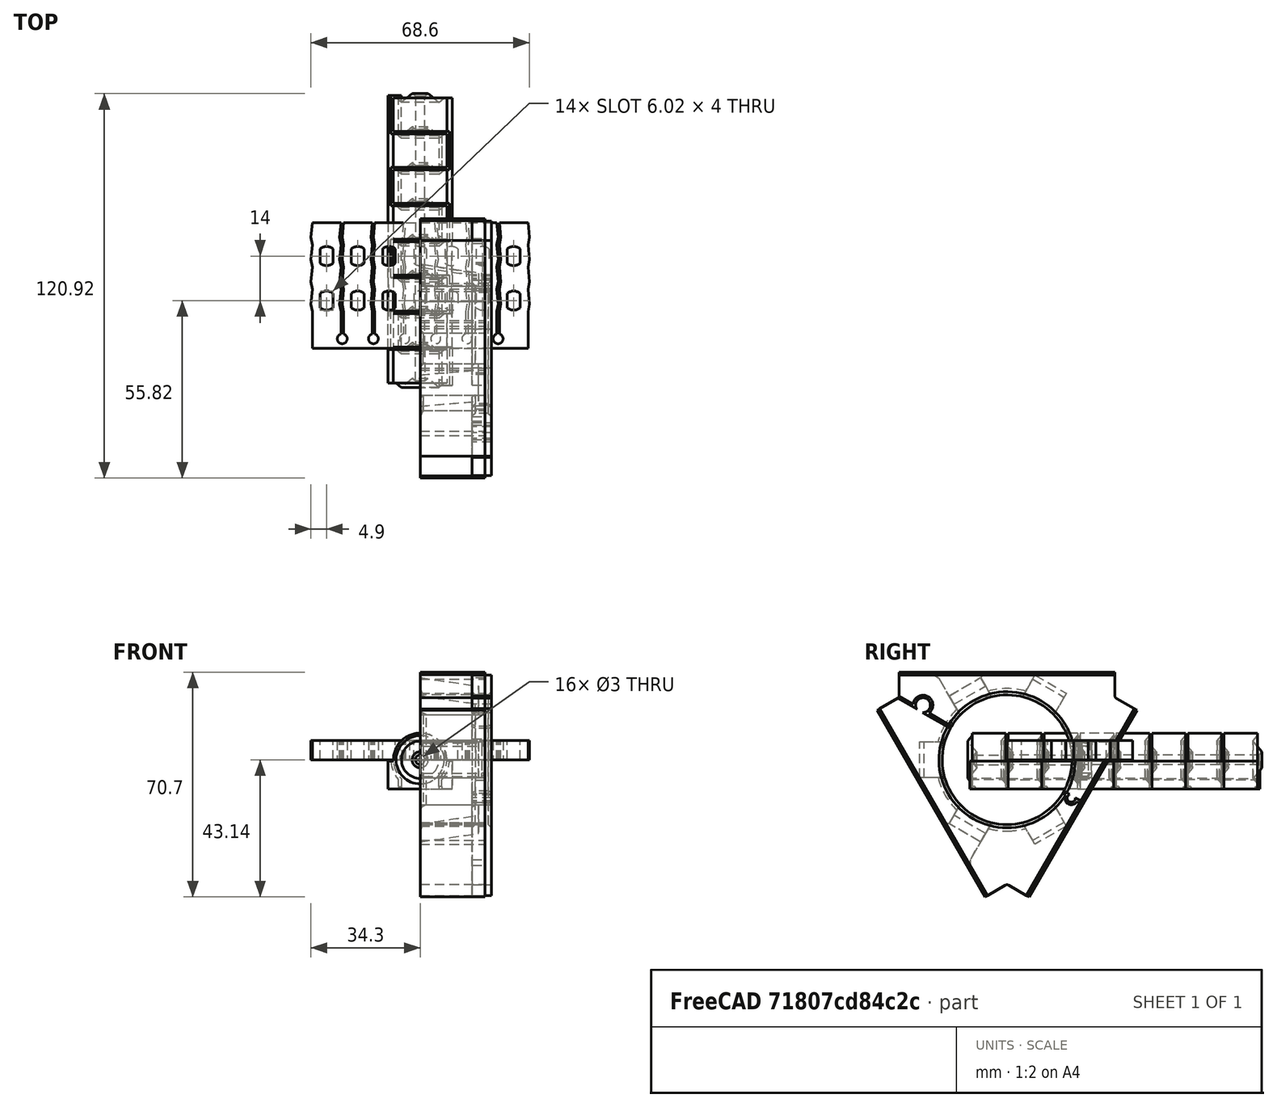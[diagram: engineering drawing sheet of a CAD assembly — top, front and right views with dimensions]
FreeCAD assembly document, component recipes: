
FREECAD ASSEMBLY — COMPONENT RECIPES ("BaseHingeModel_ver1.2_AxisFixator")

This assembly document has 8 components, labeled P0..P7 below (a component is one placed body or linked part). 7 of them carry a construction recipe — the FreeCAD feature program that regenerates the part from scratch, quoted from this document or its linked companion documents; the rest are supplied as boundary geometry only. No exploded tour is included for this assembly.
COMPONENT P0 — geometry summary ("Assembly"; no construction recipe available for this part):
  bounding box: 182.8 x 158.8 x 20.4 mm
  tessellated surface: 20,696 triangles
  volume: 9578097130411803656351970426578674498653964242418576373807381627235447409514995756881183408189511817567906541525464308833607482709359269325981809199022080 mm^3 (1616738801575943140395693637715189882977871249383409942478852649766611869419882643060896964713126329768861879254438412431142423713072396559864123359232% of its bounding box)
COMPONENT P1 — recipe-attached ("BaseHingePart", modeled in this document).
Construction recipe (the document's own serialized feature program — sketch geometry with constraints, then the solid features built on it; lengths are millimeters unless a unit is written):

FEATURE [Sketcher::SketchObject] Sketch007  label="RightCylinderScatch"
  FullyConstrained = true
  MapMode = 5
  Support = -> [XY_Plane002]
  expr: Constraints[10] = Spreadsheet.mmDiskHight
  expr: Constraints[11] = Spreadsheet.mmLedgeStep
  expr: Constraints[12] = Spreadsheet.mmLedgeStep * 2
  expr: Constraints[13] = Spreadsheet.mmLedgeStep
  expr: Constraints[14] = Spreadsheet.mmLedgeStep / 2
  expr: Constraints[16] = Spreadsheet.mmDiskLedge
  expr: Constraints[20] = Spreadsheet.mmDiskLedge * 2
  expr: Constraints[21] = Spreadsheet.mmDiskLedge
  expr: Constraints[34] = Spreadsheet.mmAirSpace / 2
  expr: Constraints[35] = Spreadsheet.mmLedgeStep / 2
  sketch-geometry (12):
    g0: LineSegment StartX=0 StartY=10.9 StartZ=0 EndX=0.84 EndY=10.9 EndZ=0
    g1: LineSegment StartX=0.84 StartY=10.9 StartZ=0 EndX=2.52 EndY=12.3 EndZ=0
    g2: LineSegment StartX=2.52 StartY=12.3 StartZ=0 EndX=5.88 EndY=9.5 EndZ=0
    g3: LineSegment StartX=5.88 StartY=9.5 StartZ=0 EndX=7.56 EndY=10.9 EndZ=0
    g4: LineSegment StartX=7.56 StartY=10.9 StartZ=0 EndX=8.4 EndY=10.9 EndZ=0
    g5: LineSegment StartX=5.88 StartY=-1 StartZ=0 EndX=2.52 EndY=1.8 EndZ=0
    g6: LineSegment StartX=2.52 StartY=1.8 StartZ=0 EndX=0.84 EndY=0.4 EndZ=0
    g7: LineSegment StartX=0.84 StartY=0.4 StartZ=0 EndX=0 EndY=0.4 EndZ=0
    g8: LineSegment StartX=0 StartY=0.4 StartZ=0 EndX=0 EndY=10.9 EndZ=0
    g9: LineSegment StartX=8.4 StartY=0.4 StartZ=0 EndX=7.56 EndY=0.4 EndZ=0
    g10: LineSegment StartX=7.56 StartY=0.4 StartZ=0 EndX=5.88 EndY=-1 EndZ=0
    g11: LineSegment StartX=8.4 StartY=10.9 StartZ=0 EndX=8.4 EndY=0.4 EndZ=0
  constraints (38):
    c: PointOnObject(g0,g-2)
    c: Horizontal(g0)
    c: Coincident(g0,g1)
    c: Coincident(g1,g2)
    c: Coincident(g2,g3)
    c: Coincident(g3,g4)
    c: Horizontal(g4)
    c: Coincident(g5,g6)
    c: Horizontal(g7)
    c: Coincident(g7,g8)
    c: DistanceY(g7,g0) = 10.5
    c: DistanceX(g0,g1) = 1.68
    c: DistanceX(g1,g2) = 3.36
    c: DistanceX(g2,g3) = 1.68
    c: DistanceX(g3,g4) = 0.84
    c: Coincident(g6,g7)
    c: DistanceY(g0,g1) = 1.4
    c: Equal(g0,g7)
    c: Equal(g1,g6)
    c: Coincident(g0,g8)
    c: DistanceY(g2,g1) = 2.8
    c: DistanceY(g2,g3) = 1.4
    c: Parallel(g2,g5)
    c: Coincident(g9,g10)
    c: Coincident(g10,g5)
    c: Parallel(g3,g10)
    c: Equal(g4,g9)
    c: Horizontal(g9)
    c: Vertical(g2,g5)
    c: Parallel(g1,g6)
    c: Vertical(g8)
    c: Coincident(g11,g4)
    c: Coincident(g11,g9)
    c: Vertical(g11)
    c: DistanceY(g-1,g7) = 0.4
    c: DistanceX(g-1,g0) = 0.84
    c: DistanceX(g-1,g0) = 0
    c: Vertical(g1,g5)
FEATURE [Sketcher::SketchObject] Sketch011  label="LeftCylinderScatch"
  FullyConstrained = true
  MapMode = 5
  Support = -> [XY_Plane]
  expr: Constraints[10] = Spreadsheet.mmLedgeStep
  expr: Constraints[11] = Spreadsheet.mmLedgeStep * 2
  expr: Constraints[12] = Spreadsheet.mmLedgeStep
  expr: Constraints[13] = Spreadsheet.mmLedgeStep / 2
  expr: Constraints[15] = Spreadsheet.mmDiskLedge
  expr: Constraints[19] = Spreadsheet.mmDiskLedge * 2
  expr: Constraints[20] = Spreadsheet.mmDiskLedge
  expr: Constraints[33] = Spreadsheet.mmAirSpace / 2
  expr: Constraints[34] = Spreadsheet.mmLedgeStep / 2
  expr: Constraints[9] = Spreadsheet.mmDiskHight
  sketch-geometry (12):
    g0: LineSegment StartX=0 StartY=-0.4 StartZ=0 EndX=0.84 EndY=-0.4 EndZ=0
    g1: LineSegment StartX=0.84 StartY=-0.4 StartZ=0 EndX=2.52 EndY=1 EndZ=0
    g2: LineSegment StartX=2.52 StartY=1 StartZ=0 EndX=5.88 EndY=-1.8 EndZ=0
    g3: LineSegment StartX=5.88 StartY=-1.8 StartZ=0 EndX=7.56 EndY=-0.4 EndZ=0
    g4: LineSegment StartX=7.56 StartY=-0.4 StartZ=0 EndX=8.4 EndY=-0.4 EndZ=0
    g5: LineSegment StartX=5.88 StartY=-12.3 StartZ=0 EndX=2.52 EndY=-9.5 EndZ=0
    g6: LineSegment StartX=2.52 StartY=-9.5 StartZ=0 EndX=0.84 EndY=-10.9 EndZ=0
    g7: LineSegment StartX=0.84 StartY=-10.9 StartZ=0 EndX=0 EndY=-10.9 EndZ=0
    g8: LineSegment StartX=0 StartY=-10.9 StartZ=0 EndX=0 EndY=-0.4 EndZ=0
    g9: LineSegment StartX=8.4 StartY=-10.9 StartZ=0 EndX=7.56 EndY=-10.9 EndZ=0
    g10: LineSegment StartX=7.56 StartY=-10.9 StartZ=0 EndX=5.88 EndY=-12.3 EndZ=0
    g11: LineSegment StartX=8.4 StartY=-0.4 StartZ=0 EndX=8.4 EndY=-10.9 EndZ=0
  constraints (36):
    c: Horizontal(g0)
    c: Coincident(g0,g1)
    c: Coincident(g1,g2)
    c: Coincident(g2,g3)
    c: Coincident(g3,g4)
    c: Horizontal(g4)
    c: Coincident(g5,g6)
    c: Horizontal(g7)
    c: Coincident(g7,g8)
    c: DistanceY(g7,g0) = 10.5
    c: DistanceX(g0,g1) = 1.68
    c: DistanceX(g1,g2) = 3.36
    c: DistanceX(g2,g3) = 1.68
    c: DistanceX(g3,g4) = 0.84
    c: Coincident(g6,g7)
    c: DistanceY(g0,g1) = 1.4
    c: Equal(g0,g7)
    c: Equal(g1,g6)
    c: Coincident(g0,g8)
    c: DistanceY(g2,g1) = 2.8
    c: DistanceY(g2,g3) = 1.4
    c: Parallel(g2,g5)
    c: Coincident(g9,g10)
    c: Coincident(g10,g5)
    c: Parallel(g3,g10)
    c: Equal(g4,g9)
    c: Horizontal(g9)
    c: Vertical(g2,g5)
    c: Parallel(g1,g6)
    c: Vertical(g8)
    c: Coincident(g11,g4)
    c: Coincident(g11,g9)
    c: Vertical(g11)
    c: DistanceY(g0,g-1) = 0.4
    c: DistanceX(g-1,g0) = 0.84
    c: DistanceX(g-1,g0) = 0
FEATURE [PartDesign::Revolution] Revolution  label="RightCylinderRevolution"
  Angle = 360
  Axis = (0,1,0)
  Base = (0,0,0)
  Profile = -> Sketch007
  ReferenceAxis = -> Sketch007 [V_Axis]
  Reversed = true
FEATURE [PartDesign::Revolution] Revolution004  label="LeftCylinderRevolution"
  Angle = 360
  Axis = (0,1,0)
  Base = (0,0,0)
  Profile = -> Sketch011
  ReferenceAxis = -> Sketch011 [V_Axis]
  Reversed = true
FEATURE [Sketcher::SketchObject] Sketch013  label="RightCylinderAxisHoleScatch"
  AttachmentOffset = pos=(0,0,1) rot=(0,0,1;0rad)
  FullyConstrained = true
  MapMode = 5
  Placement = pos=(0,-1,-2e-16) rot=(1,0,0;1.5708rad)
  Support = -> [XZ_Plane002]
  expr: .AttachmentOffset.Base.z = Spreadsheet.mmDiskLedge - Spreadsheet.mmAirSpace / 2
  expr: Constraints[1] = Spreadsheet.mmHoleRadius * 2
  sketch-geometry (1):
    g0: Circle CenterX=0 CenterY=0 CenterZ=0 NormalX=0 NormalY=0 NormalZ=1 AngleXU=0 Radius=1.5
  constraints (2):
    c: Coincident(g0,g-1)
    c: Diameter(g0) = 3
FEATURE [PartDesign::Pocket] Pocket001  label="RightCylinderAxisHole"
  BaseFeature = -> Revolution
  Direction = (0,1,2e-16)
  Length = 23.8
  Length2 = 5
  Profile = -> Sketch013
  ReferenceAxis = -> Sketch013 [N_Axis]
  Type = 0
  expr: Length = 2 * Spreadsheet.mmDiskHight + 2 * Spreadsheet.mmDiskLedge
FEATURE [Sketcher::SketchObject] Sketch014  label="LeftCylinderAxisHoleScatch"
  AttachmentOffset = pos=(0,0,-1) rot=(0,0,1;0rad)
  FullyConstrained = true
  MapMode = 5
  Placement = pos=(0,1,2e-16) rot=(1,0,0;1.5708rad)
  Support = -> [XZ_Plane]
  expr: .AttachmentOffset.Base.z = -(Spreadsheet.mmDiskLedge - Spreadsheet.mmAirSpace / 2)
  expr: Constraints[1] = Spreadsheet.mmHoleRadius * 2
  sketch-geometry (1):
    g0: Circle CenterX=0 CenterY=0 CenterZ=0 NormalX=0 NormalY=0 NormalZ=1 AngleXU=0 Radius=1.5
  constraints (2):
    c: Coincident(g0,g-1)
    c: Diameter(g0) = 3
FEATURE [PartDesign::Pocket] Pocket002  label="LeftCylinderAxisHole"
  BaseFeature = -> Revolution004
  Direction = (0,1,2e-16)
  Length = 21
  Length2 = 5
  Profile = -> Sketch014
  ReferenceAxis = -> Sketch014 [N_Axis]
  Reversed = true
  Type = 0
  expr: Length = Spreadsheet.mmDiskHight * 2
FEATURE [Sketcher::SketchObject] Sketch023  label="RightCylinderConnectedWingScatch"
  AttachmentOffset = pos=(0,0,-0.4) rot=(0,0,1;0rad)
  FullyConstrained = false
  MapMode = 5
  Placement = pos=(0,0.4,1e-16) rot=(1,0,0;1.5708rad)
  Support = -> [XZ_Plane002]
  expr: .AttachmentOffset.Base.z = -Spreadsheet.mmAirSpace / 2
  expr: Constraints[11] = Spreadsheet.mmHingeRadius + Spreadsheet.mmAirSpace
  expr: Constraints[17] = Spreadsheet.mmHingeRadius + Spreadsheet.mmAirSpace
  expr: Constraints[4] = Spreadsheet.mmHingeRadius * 2
  expr: Constraints[7] = Spreadsheet.mmHingeRadius / 5
  expr: Constraints[8] = Spreadsheet.mmAirSpace / 2
  sketch-geometry (9):
    g0: LineSegment StartX=-5.9397 StartY=-9.2 StartZ=0 EndX=10.0705 EndY=-9.2 EndZ=0
    g1: LineSegment StartX=10.0705 StartY=-9.2 StartZ=0 EndX=10.0705 EndY=-0.4 EndZ=0
    g2: LineSegment StartX=10.0705 StartY=-0.4 StartZ=0 EndX=8.39047 EndY=-0.4 EndZ=0
    g3: ArcOfCircle CenterX=0 CenterY=9e-16 CenterZ=0 NormalX=0 NormalY=0 NormalZ=1 AngleXU=0 Radius=8.4 StartAngle=3.92699 EndAngle=6.23555
    g4: LineSegment StartX=-10.8949 StartY=25.2528 StartZ=0 EndX=-10.8949 EndY=-29.472 EndZ=0
    g5: LineSegment StartX=0 StartY=0 StartZ=0 EndX=8.39047 EndY=-0.4 EndZ=0
    g6: LineSegment StartX=-5.9397 StartY=-5.9397 StartZ=0 EndX=-5.9397 EndY=-9.2 EndZ=0
    g7: LineSegment StartX=0 StartY=9e-16 StartZ=0 EndX=-20.2547 EndY=-20.2547 EndZ=0
    g8: LineSegment StartX=-5.9397 StartY=-5.9397 StartZ=0 EndX=-5.9397 EndY=-9.42884 EndZ=0
  constraints (24):
    c: Coincident(g0,g1)
    c: Vertical(g1)
    c: Horizontal(g2)
    c: Vertical(g4)
    c: Diameter(g3) = 16.8
    c: Coincident(g2,g1)
    c: Coincident(g5,g2)
    c: DistanceX(g2,g2) = 1.68
    c: DistanceY(g1,g-1) = 0.4
    c: Coincident(g3,g6)
    c: Coincident(g3,g2)
    c: DistanceY(g0,g3) = 9.2
    c: PointOnObject(g3,g7)
    c: Coincident(g7,g3)
    c: Angle(g-2,g7) = 2.35619
    c: PointOnObject(g3,g-2)
    c: Horizontal(g0)
    c: DistanceY(g0,g-1) = 9.2
    c: Vertical(g8)
    c: PointOnObject(g8,g7)
    c: PointOnObject(g8,g3)
    c: PointOnObject(g6,g8)
    c: PointOnObject(g0,g8)
    c: PointOnObject(g6,g0)
FEATURE [PartDesign::Pad] Pad008  label="RightCylinderConnectedWingBody"
  BaseFeature = -> Pocket001
  Direction = (0,-1,-2e-16)
  Length = 10.5
  Length2 = 10
  Profile = -> Sketch023
  ReferenceAxis = -> Sketch023 [N_Axis]
  Reversed = true
  Type = 0
  expr: Length = Spreadsheet.mmDiskHight
FEATURE [Sketcher::SketchObject] Sketch024  label="RightCylinderDisconnectedWingScatch"
  AttachmentOffset = pos=(0,0,0.4) rot=(0,0,1;0rad)
  FullyConstrained = false
  MapMode = 5
  Placement = pos=(0,-0.4,-1e-16) rot=(1,0,0;1.5708rad)
  Support = -> [XZ_Plane002]
  expr: .AttachmentOffset.Base.z = Spreadsheet.mmAirSpace / 2
  expr: Constraints[10] = Spreadsheet.mmHingeRadius * 6 / 5
  expr: Constraints[14] = (Spreadsheet.mmHingeRadius + Spreadsheet.mmAirSpace) * 2
  expr: Constraints[18] = Spreadsheet.mmAirSpace
  expr: Constraints[26] = Spreadsheet.mmAirSpace
  expr: Constraints[29] = Spreadsheet.mmHingeRadius * 2
  expr: Constraints[2] = (Spreadsheet.mmHingeRadius + Spreadsheet.mmAirSpace) * 2
  expr: Constraints[8] = Spreadsheet.mmHingeRadius + Spreadsheet.mmAirSpace
  expr: Constraints[9] = Spreadsheet.mmAirSpace / 2
  sketch-geometry (12):
    g0: Circle CenterX=0 CenterY=0 CenterZ=0 NormalX=0 NormalY=0 NormalZ=1 AngleXU=0 Radius=9.2
    g1: LineSegment StartX=-5.9397 StartY=-5.9397 StartZ=0 EndX=-5.9397 EndY=-9.59435 EndZ=0
    g2: LineSegment StartX=-10.08 StartY=-0.4 StartZ=0 EndX=-10.08 EndY=-9.2 EndZ=0
    g3: LineSegment StartX=-10.08 StartY=-9.2 StartZ=0 EndX=-5.9397 EndY=-9.2 EndZ=0
    g4: LineSegment StartX=-6.7397 StartY=-8.4 StartZ=0 EndX=-6.7397 EndY=-6.26231 EndZ=0
    g5: LineSegment StartX=-9.1913 StartY=-0.4 StartZ=0 EndX=-10.08 EndY=-0.4 EndZ=0
    g6: LineSegment StartX=0 StartY=0 StartZ=0 EndX=-7.18968 EndY=-7.18968 EndZ=0
    g7: ArcOfCircle CenterX=0 CenterY=0 CenterZ=0 NormalX=0 NormalY=0 NormalZ=1 AngleXU=0 Radius=9.2 StartAngle=3.18508 EndAngle=3.89029
    g8: LineSegment StartX=-6.7397 StartY=-9.55843 StartZ=0 EndX=-6.7397 EndY=-4.9559 EndZ=0
    g9: LineSegment StartX=-6.7397 StartY=-8.4 StartZ=0 EndX=-5.9397 EndY=-8.4 EndZ=0
    g10: LineSegment StartX=-5.9397 StartY=-8.4 StartZ=0 EndX=-5.9397 EndY=-9.2 EndZ=0
    g11: Circle CenterX=0 CenterY=0 CenterZ=0 NormalX=0 NormalY=0 NormalZ=1 AngleXU=0 Radius=8.4
  constraints (33):
    c: Coincident(g0,g-1)
    c: Vertical(g1)
    c: Diameter(g0) = 18.4
    c: Vertical(g2)
    c: Coincident(g2,g3)
    c: Horizontal(g3)
    c: Coincident(g5,g2)
    c: Horizontal(g5)
    c: DistanceY(g2,g-1) = 9.2
    c: DistanceY(g2,g-1) = 0.4
    c: DistanceX(g2,g0) = 10.08
    c: Coincident(g6,g0)
    c: Angle(g-2,g6) = 2.35619
    c: Coincident(g7,g0)
    c: Diameter(g7) = 18.4
    c: Coincident(g7,g4)
    c: Coincident(g7,g5)
    c: Vertical(g8)
    c: DistanceX(g8,g1) = 0.8
    c: Coincident(g4,g9)
    c: PointOnObject(g9,g1)
    c: Horizontal(g9)
    c: Coincident(g9,g10)
    c: PointOnObject(g10,g1)
    c: PointOnObject(g3,g1)
    c: PointOnObject(g10,g3)
    c: DistanceY(g3,g9) = 0.8
    c: PointOnObject(g4,g8)
    c: Coincident(g11,g7)
    c: Diameter(g11) = 16.8
    c: PointOnObject(g1,g11)
    c: PointOnObject(g1,g6)
    c: PointOnObject(g4,g8)
FEATURE [PartDesign::Pad] Pad009  label="RightCylinderDisconnectedWingBody"
  BaseFeature = -> Pad008
  Direction = (0,-1,-2e-16)
  Length = 12.1
  Length2 = 10
  Profile = -> Sketch024
  ReferenceAxis = -> Sketch024 [N_Axis]
  Reversed = true
  Type = 0
  expr: Length = Spreadsheet.mmDiskHight + Spreadsheet.mmAirSpace * 2
FEATURE [Sketcher::SketchObject] Sketch025  label="LeftCylinderConnectedWingScatch"
  AttachmentOffset = pos=(0,0,0.4) rot=(0,0,1;0rad)
  FullyConstrained = false
  MapMode = 5
  Placement = pos=(0,-0.4,-1e-16) rot=(1,0,0;1.5708rad)
  Support = -> [XZ_Plane]
  expr: .AttachmentOffset.Base.z = Spreadsheet.mmAirSpace / 2
  expr: Constraints[10] = Spreadsheet.mmAirSpace / 2
  expr: Constraints[11] = Spreadsheet.mmHingeRadius + Spreadsheet.mmAirSpace
  expr: Constraints[15] = Spreadsheet.mmHingeRadius * 2
  expr: Constraints[2] = Spreadsheet.mmHingeRadius * 2
  expr: Constraints[9] = Spreadsheet.mmHingeRadius * 6 / 5
  sketch-geometry (8):
    g0: LineSegment StartX=0 StartY=0 StartZ=0 EndX=8.8497 EndY=-8.8497 EndZ=0
    g1: Circle CenterX=0 CenterY=0 CenterZ=0 NormalX=0 NormalY=0 NormalZ=1 AngleXU=0 Radius=8.4
    g2: LineSegment StartX=-10.08 StartY=-0.4 StartZ=0 EndX=-10.08 EndY=-9.2 EndZ=0
    g3: LineSegment StartX=-10.08 StartY=-9.2 StartZ=0 EndX=5.9397 EndY=-9.2 EndZ=0
    g4: LineSegment StartX=5.9397 StartY=-9.2 StartZ=0 EndX=5.9397 EndY=-5.9397 EndZ=0
    g5: LineSegment StartX=-8.39047 StartY=-0.4 StartZ=0 EndX=-10.08 EndY=-0.4 EndZ=0
    g6: ArcOfCircle CenterX=0 CenterY=0 CenterZ=0 NormalX=0 NormalY=0 NormalZ=1 AngleXU=0 Radius=8.4 StartAngle=3.18923 EndAngle=5.49779
    g7: LineSegment StartX=5.9397 StartY=-5.9397 StartZ=0 EndX=5.9397 EndY=-9.58153 EndZ=0
  constraints (24):
    c: Coincident(g0,g-1)
    c: Coincident(g1,g0)
    c: Diameter(g1) = 16.8
    c: Vertical(g2)
    c: Coincident(g2,g3)
    c: Horizontal(g3)
    c: Coincident(g5,g2)
    c: Horizontal(g5)
    c: PointOnObject(g5,g1)
    c: DistanceX(g2,g0) = 10.08
    c: DistanceY(g2,g-1) = 0.4
    c: DistanceY(g2,g-1) = 9.2
    c: Angle(g0,g-2) = 2.35619
    c: PointOnObject(g4,g0)
    c: Coincident(g6,g0)
    c: Diameter(g6) = 16.8
    c: Coincident(g6,g5)
    c: Coincident(g6,g4)
    c: Vertical(g7)
    c: PointOnObject(g7,g1)
    c: PointOnObject(g7,g0)
    c: PointOnObject(g4,g7)
    c: PointOnObject(g3,g7)
    c: PointOnObject(g4,g3)
FEATURE [PartDesign::Pad] Pad010  label="LeftCylinderConnectedWingBody"
  BaseFeature = -> Pocket002
  Direction = (0,-1,-2e-16)
  Length = 10.5
  Length2 = 10
  Profile = -> Sketch025
  ReferenceAxis = -> Sketch025 [N_Axis]
  Type = 0
  expr: Length = Spreadsheet.mmDiskHight
FEATURE [Sketcher::SketchObject] Sketch026  label="LeftCylinderDisconnectedWingScatch"
  AttachmentOffset = pos=(0,0,-0.4) rot=(0,0,1;0rad)
  FullyConstrained = false
  MapMode = 5
  Placement = pos=(0,0.4,1e-16) rot=(1,0,0;1.5708rad)
  Support = -> [XZ_Plane]
  expr: .AttachmentOffset.Base.z = -Spreadsheet.mmAirSpace / 2
  expr: Constraints[10] = Spreadsheet.mmHingeRadius + Spreadsheet.mmAirSpace
  expr: Constraints[16] = Spreadsheet.mmAirSpace
  expr: Constraints[18] = (Spreadsheet.mmHingeRadius + Spreadsheet.mmAirSpace) * 2
  expr: Constraints[26] = Spreadsheet.mmAirSpace
  expr: Constraints[29] = Spreadsheet.mmHingeRadius * 2
  expr: Constraints[2] = (Spreadsheet.mmHingeRadius + Spreadsheet.mmAirSpace) * 2
  expr: Constraints[8] = Spreadsheet.mmAirSpace / 2
  expr: Constraints[9] = Spreadsheet.mmHingeRadius / 5 * 6
  sketch-geometry (12):
    g0: LineSegment StartX=0 StartY=0 StartZ=0 EndX=9.28474 EndY=-9.28474 EndZ=0
    g1: ArcOfCircle CenterX=0 CenterY=0 CenterZ=0 NormalX=0 NormalY=0 NormalZ=1 AngleXU=0 Radius=9.2 StartAngle=5.53449 EndAngle=6.23969
    g2: LineSegment StartX=9.1913 StartY=-0.4 StartZ=0 EndX=10.08 EndY=-0.4 EndZ=0
    g3: LineSegment StartX=10.08 StartY=-0.4 StartZ=0 EndX=10.08 EndY=-9.2 EndZ=0
    g4: LineSegment StartX=10.08 StartY=-9.2 StartZ=0 EndX=5.9397 EndY=-9.2 EndZ=0
    g5: LineSegment StartX=6.7397 StartY=-8.4 StartZ=0 EndX=6.7397 EndY=-6.26231 EndZ=0
    g6: LineSegment StartX=5.9397 StartY=-5.9397 StartZ=0 EndX=5.9397 EndY=-9.17966 EndZ=0
    g7: LineSegment StartX=6.7397 StartY=-5.451 StartZ=0 EndX=6.7397 EndY=-9.15329 EndZ=0
    g8: Circle CenterX=0 CenterY=0 CenterZ=0 NormalX=0 NormalY=0 NormalZ=1 AngleXU=0 Radius=9.2
    g9: LineSegment StartX=6.7397 StartY=-8.4 StartZ=0 EndX=5.9397 EndY=-8.4 EndZ=0
    g10: LineSegment StartX=5.9397 StartY=-8.4 StartZ=0 EndX=5.9397 EndY=-9.2 EndZ=0
    g11: Circle CenterX=0 CenterY=0 CenterZ=0 NormalX=0 NormalY=0 NormalZ=1 AngleXU=0 Radius=8.4
  constraints (33):
    c: Coincident(g0,g-1)
    c: Coincident(g1,g0)
    c: Diameter(g1) = 18.4
    c: Horizontal(g2)
    c: Coincident(g2,g3)
    c: Vertical(g3)
    c: Coincident(g3,g4)
    c: Horizontal(g4)
    c: DistanceY(g2,g-1) = 0.4
    c: DistanceX(g-1,g2) = 10.08
    c: DistanceY(g3,g-1) = 9.2
    c: Angle(g0,g-2) = 2.35619
    c: Coincident(g1,g2)
    c: Coincident(g1,g5)
    c: Vertical(g6)
    c: Vertical(g7)
    c: DistanceX(g6,g7) = 0.8
    c: Coincident(g8,g1)
    c: Diameter(g8) = 18.4
    c: PointOnObject(g5,g7)
    c: Coincident(g5,g9)
    c: PointOnObject(g9,g6)
    c: Horizontal(g9)
    c: Coincident(g9,g10)
    c: PointOnObject(g10,g6)
    c: PointOnObject(g4,g6)
    c: DistanceY(g4,g9) = 0.8
    c: PointOnObject(g10,g4)
    c: Coincident(g11,g1)
    c: Diameter(g11) = 16.8
    c: PointOnObject(g6,g11)
    c: PointOnObject(g6,g0)
    c: PointOnObject(g1,g7)
FEATURE [PartDesign::Pad] Pad011  label="LeftCylinderDisconnectedWingBody"
  BaseFeature = -> Pad010
  Direction = (0,-1,-2e-16)
  Length = 12.1
  Length2 = 10
  Profile = -> Sketch026
  ReferenceAxis = -> Sketch026 [N_Axis]
  Type = 0
  expr: Length = Spreadsheet.mmDiskHight + Spreadsheet.mmAirSpace * 2
FEATURE [Sketcher::SketchObject] Sketch046  label="LeftCylinderSeparatorScatch"
  AttachmentOffset = pos=(0,0,-0.4) rot=(0,0,1;0rad)
  FullyConstrained = false
  MapMode = 5
  Placement = pos=(0,0.4,1e-16) rot=(1,0,0;1.5708rad)
  Support = -> [XZ_Plane]
  expr: .AttachmentOffset.Base.z = -Spreadsheet.mmAirSpace / 2
  expr: Constraints[14] = Spreadsheet.mmAirSpace
  expr: Constraints[15] = Spreadsheet.mmHingeRadius * 2
  expr: Constraints[2] = Spreadsheet.mmHingeRadius + Spreadsheet.mmAirSpace
  expr: Constraints[6] = Spreadsheet.mmAirSpace
  expr: Constraints[7] = (Spreadsheet.mmHingeRadius + Spreadsheet.mmAirSpace) * 2
  sketch-geometry (9):
    g0: LineSegment StartX=0 StartY=0 StartZ=0 EndX=9.28922 EndY=-9.28922 EndZ=0
    g1: LineSegment StartX=6.7397 StartY=-9.2 StartZ=0 EndX=5.9397 EndY=-9.2 EndZ=0
    g2: LineSegment StartX=6.7397 StartY=-8.4 StartZ=0 EndX=6.7397 EndY=-9.2 EndZ=0
    g3: LineSegment StartX=5.9397 StartY=-5.9397 StartZ=0 EndX=5.9397 EndY=-8.88748 EndZ=0
    g4: LineSegment StartX=6.7397 StartY=-5.40605 StartZ=0 EndX=6.7397 EndY=-8.88997 EndZ=0
    g5: Circle CenterX=0 CenterY=0 CenterZ=0 NormalX=0 NormalY=0 NormalZ=1 AngleXU=0 Radius=9.2
    g6: LineSegment StartX=6.7397 StartY=-8.4 StartZ=0 EndX=5.9397 EndY=-8.4 EndZ=0
    g7: LineSegment StartX=5.9397 StartY=-8.4 StartZ=0 EndX=5.9397 EndY=-9.2 EndZ=0
    g8: Circle CenterX=0 CenterY=0 CenterZ=0 NormalX=0 NormalY=0 NormalZ=1 AngleXU=0 Radius=8.4
  constraints (23):
    c: Coincident(g0,g-1)
    c: Horizontal(g1)
    c: DistanceY(g1,g-1) = 9.2
    c: Angle(g0,g-2) = 2.35619
    c: Vertical(g3)
    c: Vertical(g4)
    c: DistanceX(g3,g4) = 0.8
    c: Diameter(g5) = 18.4
    c: PointOnObject(g2,g4)
    c: Coincident(g2,g6)
    c: PointOnObject(g6,g3)
    c: Horizontal(g6)
    c: Coincident(g6,g7)
    c: PointOnObject(g7,g3)
    c: DistanceY(g1,g6) = 0.8
    c: Diameter(g8) = 16.8
    c: PointOnObject(g3,g8)
    c: PointOnObject(g3,g0)
    c: PointOnObject(g1,g4)
    c: Coincident(g2,g1)
    c: Coincident(g0,g8)
    c: Coincident(g0,g5)
    c: Coincident(g7,g1)
FEATURE [PartDesign::Pocket] Pocket004  label="LeftCylinderSeparator"
  BaseFeature = -> Pad011
  Direction = (0,1,2e-16)
  Length = 10.5
  Length2 = 5
  Profile = -> Sketch046
  ReferenceAxis = -> Sketch046 [N_Axis]
  Reversed = true
  Type = 0
  expr: Length = Spreadsheet.mmDiskHight
FEATURE [PartDesign::Body] Body  label="LeftCylinder"
  Group = -> [Sketch011,Revolution004,Sketch014,Pocket002,Sketch025,Pad010,Sketch026,Pad011,Sketch046,Pocket004]
  Origin = -> Origin
  Tip = -> Pocket004
FEATURE [Sketcher::SketchObject] Sketch047  label="RightCylinderSeparatorScatch"
  AttachmentOffset = pos=(0,0,0.4) rot=(0,0,1;0rad)
  FullyConstrained = false
  MapMode = 5
  Placement = pos=(0,-0.4,-1e-16) rot=(1,0,0;1.5708rad)
  Support = -> [XZ_Plane002]
  expr: .AttachmentOffset.Base.z = Spreadsheet.mmAirSpace / 2
  expr: Constraints[15] = Spreadsheet.mmAirSpace
  expr: Constraints[17] = Spreadsheet.mmHingeRadius * 2
  expr: Constraints[2] = (Spreadsheet.mmHingeRadius + Spreadsheet.mmAirSpace) * 2
  expr: Constraints[4] = Spreadsheet.mmHingeRadius + Spreadsheet.mmAirSpace
  expr: Constraints[8] = Spreadsheet.mmAirSpace
  sketch-geometry (9):
    g0: Circle CenterX=0 CenterY=0 CenterZ=0 NormalX=0 NormalY=0 NormalZ=1 AngleXU=0 Radius=9.2
    g1: LineSegment StartX=-5.9397 StartY=-5.9397 StartZ=0 EndX=-5.9397 EndY=-9.59435 EndZ=0
    g2: LineSegment StartX=-6.7397 StartY=-9.2 StartZ=0 EndX=-5.9397 EndY=-9.2 EndZ=0
    g3: LineSegment StartX=0 StartY=0 StartZ=0 EndX=-7.19425 EndY=-7.19425 EndZ=0
    g4: LineSegment StartX=-6.7397 StartY=-9.55843 StartZ=0 EndX=-6.7397 EndY=-4.9559 EndZ=0
    g5: LineSegment StartX=-6.7397 StartY=-8.4 StartZ=0 EndX=-5.9397 EndY=-8.4 EndZ=0
    g6: LineSegment StartX=-5.9397 StartY=-8.4 StartZ=0 EndX=-5.9397 EndY=-9.2 EndZ=0
    g7: Circle CenterX=0 CenterY=0 CenterZ=0 NormalX=0 NormalY=0 NormalZ=1 AngleXU=0 Radius=8.4
    g8: LineSegment StartX=-6.7397 StartY=-8.4 StartZ=0 EndX=-6.7397 EndY=-9.2 EndZ=0
  constraints (24):
    c: Coincident(g0,g-1)
    c: Vertical(g1)
    c: Diameter(g0) = 18.4
    c: Horizontal(g2)
    c: DistanceY(g2,g-1) = 9.2
    c: Coincident(g3,g0)
    c: Angle(g-2,g3) = 2.35619
    c: Vertical(g4)
    c: DistanceX(g4,g1) = 0.8
    c: PointOnObject(g5,g1)
    c: Horizontal(g5)
    c: Coincident(g5,g6)
    c: PointOnObject(g6,g1)
    c: PointOnObject(g2,g1)
    c: PointOnObject(g6,g2)
    c: DistanceY(g2,g5) = 0.8
    c: PointOnObject(g5,g4)
    c: Diameter(g7) = 16.8
    c: PointOnObject(g1,g7)
    c: PointOnObject(g1,g3)
    c: PointOnObject(g2,g4)
    c: Coincident(g8,g5)
    c: Coincident(g8,g2)
    c: Coincident(g0,g7)
FEATURE [PartDesign::Pocket] Pocket005  label="RightCylinderSeparator"
  BaseFeature = -> Pad009
  Direction = (0,1,2e-16)
  Length = 10.5
  Length2 = 5
  Profile = -> Sketch047
  ReferenceAxis = -> Sketch047 [N_Axis]
  Type = 0
  expr: Length = Spreadsheet.mmDiskHight
FEATURE [PartDesign::Body] Body001  label="RightCylinder"
  Group = -> [Sketch007,Revolution,Sketch013,Pocket001,Sketch023,Pad008,Sketch024,Pad009,Sketch047,Pocket005]
  Origin = -> Origin002
  Tip = -> Pocket005
COMPONENT P2 — recipe-attached ("BeamFixatoPart", modeled in this document).
Construction recipe (the document's own serialized feature program — sketch geometry with constraints, then the solid features built on it; lengths are millimeters unless a unit is written):

FEATURE [Sketcher::SketchObject] Sketch022  label="FixatorBodySketch"
  FullyConstrained = false
  MapMode = 5
  Support = -> [XY_Plane005]
  expr: Constraints[143] = Spreadsheet.mmCellWall
  expr: Constraints[144] = Spreadsheet.mmCellWall
  expr: Constraints[145] = Spreadsheet.mmCellWall
  expr: Constraints[146] = Spreadsheet.mmCellWidth
  expr: Constraints[147] = Spreadsheet.mmCellWidth
  expr: Constraints[148] = Spreadsheet.mmCellWidth
  expr: Constraints[169] = Spreadsheet.mmCommonBaseLenght
  expr: Constraints[170] = Spreadsheet.mmToothStep
  expr: Constraints[171] = Spreadsheet.mmToothStep
  expr: Constraints[172] = Spreadsheet.mmToothStep
  expr: Constraints[173] = Spreadsheet.mmToothStep
  expr: Constraints[174] = Spreadsheet.mmToothStep
  expr: Constraints[183] = Spreadsheet.mmCellWall * 3
  expr: Constraints[184] = Spreadsheet.mmCellWall * 3
  expr: Constraints[185] = Spreadsheet.mmCellWall * 3
  expr: Constraints[186] = Spreadsheet.mmCellWall * 3
  expr: Constraints[425] = Spreadsheet.mmFirstCircleArcToBase
  expr: Constraints[435] = Spreadsheet.mmCellWall / 2
  expr: Constraints[464] = Spreadsheet.mmCellWidth + Spreadsheet.mmCellWall
  expr: Constraints[5] = Spreadsheet.mmBaseWidth
  expr: Constraints[6] = Spreadsheet.mmBaseEnd
  sketch-geometry (155):
    g0: LineSegment StartX=-33.9 StartY=0 StartZ=0 EndX=-33.9 EndY=39.5 EndZ=0
    g1: LineSegment StartX=-33.9 StartY=39.5 StartZ=0 EndX=33.9 EndY=39.5 EndZ=0
    g2: LineSegment StartX=33.9 StartY=39.5 StartZ=0 EndX=33.9 EndY=0 EndZ=0
    g3: LineSegment StartX=-73.1099 StartY=25.5 StartZ=0 EndX=65.6354 EndY=25.5 EndZ=0
    g4: LineSegment StartX=-33.9 StartY=0 StartZ=0 EndX=-33.9 EndY=11.5 EndZ=0
    g5: LineSegment StartX=-33.9 StartY=11.5 StartZ=0 EndX=-34.3 EndY=13.9 EndZ=0
    g6: LineSegment StartX=-34.3 StartY=13.9 StartZ=0 EndX=-33.9 EndY=18.5 EndZ=0
    g7: LineSegment StartX=-33.9 StartY=18.5 StartZ=0 EndX=-34.3 EndY=20.9 EndZ=0
    g8: LineSegment StartX=-34.3 StartY=20.9 StartZ=0 EndX=-33.9 EndY=25.5 EndZ=0
    g9: LineSegment StartX=-33.9 StartY=25.5 StartZ=0 EndX=-34.3 EndY=27.9 EndZ=0
    g10: LineSegment StartX=-34.3 StartY=27.9 StartZ=0 EndX=-33.9 EndY=32.5 EndZ=0
    g11: LineSegment StartX=-33.9 StartY=32.5 StartZ=0 EndX=-34.3 EndY=34.9 EndZ=0
    g12: LineSegment StartX=-34.3 StartY=34.9 StartZ=0 EndX=-33.9 EndY=39.5 EndZ=0
    g13: LineSegment StartX=-33.9 StartY=39.5 StartZ=0 EndX=-24.9 EndY=39.5 EndZ=0
    g14: LineSegment StartX=-24.9 StartY=39.5 StartZ=0 EndX=-25.3 EndY=34.9 EndZ=0
    g15: LineSegment StartX=-25.3 StartY=34.9 StartZ=0 EndX=-24.9 EndY=32.5 EndZ=0
    g16: LineSegment StartX=-24.9 StartY=32.5 StartZ=0 EndX=-25.3 EndY=27.9 EndZ=0
    g17: LineSegment StartX=-25.3 StartY=27.9 StartZ=0 EndX=-24.9 EndY=25.5 EndZ=0
    g18: LineSegment StartX=-24.9 StartY=25.5 StartZ=0 EndX=-25.3 EndY=20.9 EndZ=0
    g19: LineSegment StartX=-25.3 StartY=20.9 StartZ=0 EndX=-24.9 EndY=18.5 EndZ=0
    g20: LineSegment StartX=-24.9 StartY=18.5 StartZ=0 EndX=-25.3 EndY=13.9 EndZ=0
    g21: LineSegment StartX=-25.3 StartY=13.9 StartZ=0 EndX=-24.9 EndY=11.5 EndZ=0
    g22: LineSegment StartX=-24.9 StartY=11.5 StartZ=0 EndX=-24.9 EndY=4.5 EndZ=0
    g23: LineSegment StartX=-24.1 StartY=4.5 StartZ=0 EndX=-24.1 EndY=11.5 EndZ=0
    g24: LineSegment StartX=-24.1 StartY=11.5 StartZ=0 EndX=-24.5 EndY=13.9 EndZ=0
    g25: LineSegment StartX=-24.5 StartY=13.9 StartZ=0 EndX=-24.1 EndY=18.5 EndZ=0
    g26: LineSegment StartX=-24.1 StartY=18.5 StartZ=0 EndX=-24.5 EndY=20.9 EndZ=0
    g27: LineSegment StartX=-24.5 StartY=20.9 StartZ=0 EndX=-24.1 EndY=25.5 EndZ=0
    g28: LineSegment StartX=-24.1 StartY=25.5 StartZ=0 EndX=-24.5 EndY=27.9 EndZ=0
    g29: LineSegment StartX=-24.5 StartY=27.9 StartZ=0 EndX=-24.1 EndY=32.5 EndZ=0
    g30: LineSegment StartX=-24.1 StartY=32.5 StartZ=0 EndX=-24.5 EndY=34.9 EndZ=0
    g31: LineSegment StartX=-24.5 StartY=34.9 StartZ=0 EndX=-24.1 EndY=39.5 EndZ=0
    g32: LineSegment StartX=-24.1 StartY=39.5 StartZ=0 EndX=-15.1 EndY=39.5 EndZ=0
    g33: LineSegment StartX=-15.1 StartY=39.5 StartZ=0 EndX=-15.5 EndY=34.9 EndZ=0
    g34: LineSegment StartX=-15.5 StartY=34.9 StartZ=0 EndX=-15.1 EndY=32.5 EndZ=0
    g35: LineSegment StartX=-15.1 StartY=32.5 StartZ=0 EndX=-15.5 EndY=27.9 EndZ=0
    g36: LineSegment StartX=-15.5 StartY=27.9 StartZ=0 EndX=-15.1 EndY=25.5 EndZ=0
    g37: LineSegment StartX=-15.1 StartY=25.5 StartZ=0 EndX=-15.5 EndY=20.9 EndZ=0
    g38: LineSegment StartX=-15.5 StartY=20.9 StartZ=0 EndX=-15.1 EndY=18.5 EndZ=0
    g39: LineSegment StartX=-15.1 StartY=18.5 StartZ=0 EndX=-15.5 EndY=13.9 EndZ=0
    g40: LineSegment StartX=-15.5 StartY=13.9 StartZ=0 EndX=-15.1 EndY=11.5 EndZ=0
    g41: LineSegment StartX=-15.1 StartY=11.5 StartZ=0 EndX=-15.1 EndY=4.5 EndZ=0
    g42: LineSegment StartX=-14.3 StartY=4.5 StartZ=0 EndX=-14.3 EndY=11.5 EndZ=0
    g43: LineSegment StartX=-14.3 StartY=11.5 StartZ=0 EndX=-14.7 EndY=13.9 EndZ=0
    g44: LineSegment StartX=-14.7 StartY=13.9 StartZ=0 EndX=-14.3 EndY=18.5 EndZ=0
    g45: LineSegment StartX=-14.3 StartY=18.5 StartZ=0 EndX=-14.7 EndY=20.9 EndZ=0
    g46: LineSegment StartX=-14.7 StartY=20.9 StartZ=0 EndX=-14.3 EndY=25.5 EndZ=0
    g47: LineSegment StartX=-14.3 StartY=25.5 StartZ=0 EndX=-14.7 EndY=27.9 EndZ=0
    g48: LineSegment StartX=-14.7 StartY=27.9 StartZ=0 EndX=-14.3 EndY=32.5 EndZ=0
    g49: LineSegment StartX=-14.3 StartY=32.5 StartZ=0 EndX=-14.7 EndY=34.9 EndZ=0
    g50: LineSegment StartX=-14.7 StartY=34.9 StartZ=0 EndX=-14.3 EndY=39.5 EndZ=0
    g51: LineSegment StartX=-14.3 StartY=39.5 StartZ=0 EndX=-5.3 EndY=39.5 EndZ=0
    g52: LineSegment StartX=-5.3 StartY=39.5 StartZ=0 EndX=-5.7 EndY=34.9 EndZ=0
    g53: LineSegment StartX=-5.7 StartY=34.9 StartZ=0 EndX=-5.3 EndY=32.5 EndZ=0
    g54: LineSegment StartX=-5.3 StartY=32.5 StartZ=0 EndX=-5.7 EndY=27.9 EndZ=0
    g55: LineSegment StartX=-5.7 StartY=27.9 StartZ=0 EndX=-5.3 EndY=25.5 EndZ=0
    g56: LineSegment StartX=-5.3 StartY=25.5 StartZ=0 EndX=-5.7 EndY=20.9 EndZ=0
    g57: LineSegment StartX=-5.7 StartY=20.9 StartZ=0 EndX=-5.3 EndY=18.5 EndZ=0
    g58: LineSegment StartX=-5.3 StartY=18.5 StartZ=0 EndX=-5.7 EndY=13.9 EndZ=0
    g59: LineSegment StartX=-5.7 StartY=13.9 StartZ=0 EndX=-5.3 EndY=11.5 EndZ=0
    g60: LineSegment StartX=-5.3 StartY=11.5 StartZ=0 EndX=-5.3 EndY=4.5 EndZ=0
    g61: LineSegment StartX=-4.5 StartY=4.5 StartZ=0 EndX=-4.5 EndY=11.5 EndZ=0
    g62: LineSegment StartX=-4.5 StartY=11.5 StartZ=0 EndX=-4.9 EndY=13.9 EndZ=0
    g63: LineSegment StartX=-4.9 StartY=13.9 StartZ=0 EndX=-4.5 EndY=18.5 EndZ=0
    g64: LineSegment StartX=-4.5 StartY=18.5 StartZ=0 EndX=-4.9 EndY=20.9 EndZ=0
    g65: LineSegment StartX=-4.9 StartY=20.9 StartZ=0 EndX=-4.5 EndY=25.5 EndZ=0
    g66: LineSegment StartX=-4.5 StartY=25.5 StartZ=0 EndX=-4.9 EndY=27.9 EndZ=0
    g67: LineSegment StartX=-4.9 StartY=27.9 StartZ=0 EndX=-4.5 EndY=32.5 EndZ=0
    g68: LineSegment StartX=-4.5 StartY=32.5 StartZ=0 EndX=-4.9 EndY=34.9 EndZ=0
    g69: LineSegment StartX=-4.9 StartY=34.9 StartZ=0 EndX=-4.5 EndY=39.5 EndZ=0
    g70: LineSegment StartX=-4.5 StartY=39.5 StartZ=0 EndX=4.5 EndY=39.5 EndZ=0
    g71: LineSegment StartX=4.5 StartY=39.5 StartZ=0 EndX=4.9 EndY=34.9 EndZ=0
    g72: LineSegment StartX=4.9 StartY=34.9 StartZ=0 EndX=4.5 EndY=32.5 EndZ=0
    g73: LineSegment StartX=4.5 StartY=32.5 StartZ=0 EndX=4.9 EndY=27.9 EndZ=0
    g74: LineSegment StartX=4.9 StartY=27.9 StartZ=0 EndX=4.5 EndY=25.5 EndZ=0
    g75: LineSegment StartX=4.5 StartY=25.5 StartZ=0 EndX=4.9 EndY=20.9 EndZ=0
    g76: LineSegment StartX=4.9 StartY=20.9 StartZ=0 EndX=4.5 EndY=18.5 EndZ=0
    g77: LineSegment StartX=4.5 StartY=18.5 StartZ=0 EndX=4.9 EndY=13.9 EndZ=0
    g78: LineSegment StartX=4.9 StartY=13.9 StartZ=0 EndX=4.5 EndY=11.5 EndZ=0
    g79: LineSegment StartX=4.5 StartY=11.5 StartZ=0 EndX=4.5 EndY=4.5 EndZ=0
    g80: LineSegment StartX=5.3 StartY=4.5 StartZ=0 EndX=5.3 EndY=11.5 EndZ=0
    g81: LineSegment StartX=5.3 StartY=11.5 StartZ=0 EndX=5.7 EndY=13.9 EndZ=0
    g82: LineSegment StartX=5.7 StartY=13.9 StartZ=0 EndX=5.3 EndY=18.5 EndZ=0
    g83: LineSegment StartX=5.3 StartY=18.5 StartZ=0 EndX=5.7 EndY=20.9 EndZ=0
    g84: LineSegment StartX=5.7 StartY=20.9 StartZ=0 EndX=5.3 EndY=25.5 EndZ=0
    g85: LineSegment StartX=5.3 StartY=25.5 StartZ=0 EndX=5.7 EndY=27.9 EndZ=0
    g86: LineSegment StartX=5.7 StartY=27.9 StartZ=0 EndX=5.3 EndY=32.5 EndZ=0
    g87: LineSegment StartX=5.3 StartY=32.5 StartZ=0 EndX=5.7 EndY=34.9 EndZ=0
    g88: LineSegment StartX=5.7 StartY=34.9 StartZ=0 EndX=5.3 EndY=39.5 EndZ=0
    g89: LineSegment StartX=5.3 StartY=39.5 StartZ=0 EndX=14.3 EndY=39.5 EndZ=0
    g90: LineSegment StartX=14.3 StartY=39.5 StartZ=0 EndX=14.7 EndY=34.9 EndZ=0
    g91: LineSegment StartX=14.7 StartY=34.9 StartZ=0 EndX=14.3 EndY=32.5 EndZ=0
    g92: LineSegment StartX=14.3 StartY=32.5 StartZ=0 EndX=14.7 EndY=27.9 EndZ=0
    g93: LineSegment StartX=14.7 StartY=27.9 StartZ=0 EndX=14.3 EndY=25.5 EndZ=0
    g94: LineSegment StartX=14.3 StartY=25.5 StartZ=0 EndX=14.7 EndY=20.9 EndZ=0
    g95: LineSegment StartX=14.7 StartY=20.9 StartZ=0 EndX=14.3 EndY=18.5 EndZ=0
    g96: LineSegment StartX=14.3 StartY=18.5 StartZ=0 EndX=14.7 EndY=13.9 EndZ=0
    g97: LineSegment StartX=14.7 StartY=13.9 StartZ=0 EndX=14.3 EndY=11.5 EndZ=0
    g98: LineSegment StartX=14.3 StartY=11.5 StartZ=0 EndX=14.3 EndY=4.5 EndZ=0
    g99: LineSegment StartX=15.1 StartY=4.5 StartZ=0 EndX=15.1 EndY=11.5 EndZ=0
    g100: LineSegment StartX=15.1 StartY=11.5 StartZ=0 EndX=15.5 EndY=13.9 EndZ=0
    g101: LineSegment StartX=15.5 StartY=13.9 StartZ=0 EndX=15.1 EndY=18.5 EndZ=0
    g102: LineSegment StartX=15.1 StartY=18.5 StartZ=0 EndX=15.5 EndY=20.9 EndZ=0
    g103: LineSegment StartX=15.5 StartY=20.9 StartZ=0 EndX=15.1 EndY=25.5 EndZ=0
    g104: LineSegment StartX=15.1 StartY=25.5 StartZ=0 EndX=15.5 EndY=27.9 EndZ=0
    g105: LineSegment StartX=15.5 StartY=27.9 StartZ=0 EndX=15.1 EndY=32.5 EndZ=0
    g106: LineSegment StartX=15.1 StartY=32.5 StartZ=0 EndX=15.5 EndY=34.9 EndZ=0
    g107: LineSegment StartX=15.5 StartY=34.9 StartZ=0 EndX=15.1 EndY=39.5 EndZ=0
    g108: LineSegment StartX=15.1 StartY=39.5 StartZ=0 EndX=24.1 EndY=39.5 EndZ=0
    g109: LineSegment StartX=24.1 StartY=39.5 StartZ=0 EndX=24.5 EndY=34.9 EndZ=0
    g110: LineSegment StartX=24.5 StartY=34.9 StartZ=0 EndX=24.1 EndY=32.5 EndZ=0
    g111: LineSegment StartX=24.1 StartY=32.5 StartZ=0 EndX=24.5 EndY=27.9 EndZ=0
    g112: LineSegment StartX=24.5 StartY=27.9 StartZ=0 EndX=24.1 EndY=25.5 EndZ=0
    g113: LineSegment StartX=24.1 StartY=25.5 StartZ=0 EndX=24.5 EndY=20.9 EndZ=0
    g114: LineSegment StartX=24.5 StartY=20.9 StartZ=0 EndX=24.1 EndY=18.5 EndZ=0
    g115: LineSegment StartX=24.1 StartY=18.5 StartZ=0 EndX=24.5 EndY=13.9 EndZ=0
    g116: LineSegment StartX=24.5 StartY=13.9 StartZ=0 EndX=24.1 EndY=11.5 EndZ=0
    g117: LineSegment StartX=24.1 StartY=11.5 StartZ=0 EndX=24.1 EndY=4.5 EndZ=0
    g118: LineSegment StartX=24.9 StartY=4.5 StartZ=0 EndX=24.9 EndY=11.5 EndZ=0
    g119: LineSegment StartX=24.9 StartY=11.5 StartZ=0 EndX=25.3 EndY=13.9 EndZ=0
    g120: LineSegment StartX=25.3 StartY=13.9 StartZ=0 EndX=24.9 EndY=18.5 EndZ=0
    g121: LineSegment StartX=24.9 StartY=18.5 StartZ=0 EndX=25.3 EndY=20.9 EndZ=0
    g122: LineSegment StartX=25.3 StartY=20.9 StartZ=0 EndX=24.9 EndY=25.5 EndZ=0
    g123: LineSegment StartX=24.9 StartY=25.5 StartZ=0 EndX=25.3 EndY=27.9 EndZ=0
    g124: LineSegment StartX=25.3 StartY=27.9 StartZ=0 EndX=24.9 EndY=32.5 EndZ=0
    g125: LineSegment StartX=24.9 StartY=32.5 StartZ=0 EndX=25.3 EndY=34.9 EndZ=0
    g126: LineSegment StartX=25.3 StartY=34.9 StartZ=0 EndX=24.9 EndY=39.5 EndZ=0
    g127: LineSegment StartX=24.9 StartY=39.5 StartZ=0 EndX=33.9 EndY=39.5 EndZ=0
    g128: LineSegment StartX=33.9 StartY=39.5 StartZ=0 EndX=34.3 EndY=34.9 EndZ=0
    g129: LineSegment StartX=34.3 StartY=34.9 StartZ=0 EndX=33.9 EndY=32.5 EndZ=0
    g130: LineSegment StartX=33.9 StartY=32.5 StartZ=0 EndX=34.3 EndY=27.9 EndZ=0
    g131: LineSegment StartX=34.3 StartY=27.9 StartZ=0 EndX=33.9 EndY=25.5 EndZ=0
    g132: LineSegment StartX=33.9 StartY=25.5 StartZ=0 EndX=34.3 EndY=20.9 EndZ=0
    g133: LineSegment StartX=34.3 StartY=20.9 StartZ=0 EndX=33.9 EndY=18.5 EndZ=0
    g134: LineSegment StartX=33.9 StartY=18.5 StartZ=0 EndX=34.3 EndY=13.9 EndZ=0
    g135: LineSegment StartX=34.3 StartY=13.9 StartZ=0 EndX=33.9 EndY=11.5 EndZ=0
    g136: LineSegment StartX=33.9 StartY=11.5 StartZ=0 EndX=33.9 EndY=0 EndZ=0
    g137: LineSegment StartX=33.9 StartY=0 StartZ=0 EndX=-33.9 EndY=0 EndZ=0
    g138: LineSegment StartX=-73.1099 StartY=18.5 StartZ=0 EndX=65.6354 EndY=18.5 EndZ=0
    g139: LineSegment StartX=-73.1099 StartY=34.9 StartZ=0 EndX=65.6354 EndY=34.9 EndZ=0
    g140: LineSegment StartX=-73.1099 StartY=32.5 StartZ=0 EndX=65.6354 EndY=32.5 EndZ=0
    g141: LineSegment StartX=-73.1099 StartY=27.9 StartZ=0 EndX=65.6354 EndY=27.9 EndZ=0
    g142: LineSegment StartX=-73.1099 StartY=20.9 StartZ=0 EndX=65.6354 EndY=20.9 EndZ=0
    g143: LineSegment StartX=-73.1099 StartY=11.5 StartZ=0 EndX=65.6354 EndY=11.5 EndZ=0
    g144: LineSegment StartX=-34.3 StartY=8.59208 StartZ=0 EndX=-34.3 EndY=49.4346 EndZ=0
    g145: LineSegment StartX=-73.1099 StartY=13.9 StartZ=0 EndX=65.6354 EndY=13.9 EndZ=0
    g146: LineSegment StartX=-33.9 StartY=0 StartZ=0 EndX=33.9 EndY=0 EndZ=0
    g147: LineSegment StartX=-73.1099 StartY=4.5 StartZ=0 EndX=65.6354 EndY=4.5 EndZ=0
    g148: ArcOfCircle CenterX=-24.5 CenterY=3 CenterZ=0 NormalX=0 NormalY=0 NormalZ=1 AngleXU=0 Radius=1.55242 StartAngle=1.8314 EndAngle=7.59338
    g149: ArcOfCircle CenterX=-14.7 CenterY=3 CenterZ=0 NormalX=0 NormalY=0 NormalZ=1 AngleXU=0 Radius=1.55242 StartAngle=1.8314 EndAngle=7.59338
    g150: ArcOfCircle CenterX=-4.9 CenterY=3 CenterZ=0 NormalX=0 NormalY=0 NormalZ=1 AngleXU=0 Radius=1.55242 StartAngle=1.8314 EndAngle=7.59338
    g151: ArcOfCircle CenterX=4.9 CenterY=3 CenterZ=0 NormalX=0 NormalY=0 NormalZ=1 AngleXU=0 Radius=1.55242 StartAngle=1.8314 EndAngle=7.59338
    g152: ArcOfCircle CenterX=14.7 CenterY=3 CenterZ=0 NormalX=0 NormalY=0 NormalZ=1 AngleXU=0 Radius=1.55242 StartAngle=1.8314 EndAngle=7.59338
    g153: ArcOfCircle CenterX=24.5 CenterY=3 CenterZ=0 NormalX=0 NormalY=0 NormalZ=1 AngleXU=0 Radius=1.55242 StartAngle=1.8314 EndAngle=7.59338
    g154: LineSegment StartX=-73.1099 StartY=3 StartZ=0 EndX=65.6354 EndY=3 EndZ=0
  constraints (469):
    c: Coincident(g0,g1)
    c: Coincident(g1,g2)
    c: Horizontal(g3)
    c: Symmetric(g0,g2,g-2)
    c: Symmetric(g1,g0,g-2)
    c: DistanceX(g0,g2) = 67.8
    c: DistanceX(g0,g1) = 67.8
    c: Coincident(g4,g5)
    c: Coincident(g5,g6)
    c: Coincident(g6,g7)
    c: Coincident(g7,g8)
    c: Coincident(g8,g9)
    c: Coincident(g9,g10)
    c: Coincident(g10,g11)
    c: Coincident(g11,g12)
    c: Coincident(g12,g13)
    c: Horizontal(g13)
    c: Coincident(g13,g14)
    c: Coincident(g14,g15)
    c: Coincident(g15,g16)
    c: Coincident(g16,g17)
    c: Coincident(g17,g18)
    c: Coincident(g18,g19)
    c: Coincident(g19,g20)
    c: Coincident(g20,g21)
    c: Coincident(g21,g22)
    c: Coincident(g23,g24)
    c: Coincident(g24,g25)
    c: Coincident(g25,g26)
    c: Coincident(g26,g27)
    c: Coincident(g27,g28)
    c: Coincident(g28,g29)
    c: Coincident(g29,g30)
    c: Coincident(g30,g31)
    c: Coincident(g31,g32)
    c: Horizontal(g32)
    c: Coincident(g32,g33)
    c: Coincident(g33,g34)
    c: Coincident(g34,g35)
    c: Coincident(g35,g36)
    c: Coincident(g36,g37)
    c: Coincident(g37,g38)
    c: Coincident(g38,g39)
    c: Coincident(g39,g40)
    c: Coincident(g40,g41)
    c: Coincident(g42,g43)
    c: Coincident(g43,g44)
    c: Coincident(g44,g45)
    c: Coincident(g45,g46)
    c: Coincident(g46,g47)
    c: Coincident(g47,g48)
    c: Coincident(g48,g49)
    c: Coincident(g49,g50)
    c: Coincident(g50,g51)
    c: Coincident(g51,g52)
    c: Coincident(g52,g53)
    c: Coincident(g53,g54)
    c: Coincident(g54,g55)
    c: Coincident(g55,g56)
    c: Coincident(g56,g57)
    c: Coincident(g57,g58)
    c: Coincident(g58,g59)
    c: Coincident(g59,g60)
    c: Coincident(g61,g62)
    c: Coincident(g62,g63)
    c: Coincident(g63,g64)
    c: Coincident(g64,g65)
    c: Coincident(g65,g66)
    c: Coincident(g66,g67)
    c: Coincident(g67,g68)
    c: Coincident(g68,g69)
    c: Coincident(g69,g70)
    c: Coincident(g70,g71)
    c: Coincident(g71,g72)
    c: Coincident(g72,g73)
    c: Coincident(g73,g74)
    c: Coincident(g74,g75)
    c: Coincident(g75,g76)
    c: Coincident(g76,g77)
    c: Coincident(g77,g78)
    c: Coincident(g78,g79)
    c: Coincident(g80,g81)
    c: Coincident(g81,g82)
    c: Coincident(g82,g83)
    c: Coincident(g83,g84)
    c: Coincident(g84,g85)
    c: Coincident(g85,g86)
    c: Coincident(g86,g87)
    c: Coincident(g87,g88)
    c: Coincident(g88,g89)
    c: Horizontal(g89)
    c: Coincident(g89,g90)
    c: Coincident(g90,g91)
    c: Coincident(g91,g92)
    c: Coincident(g92,g93)
    c: Coincident(g93,g94)
    c: Coincident(g94,g95)
    c: Coincident(g95,g96)
    c: Coincident(g96,g97)
    c: Coincident(g97,g98)
    c: Coincident(g99,g100)
    c: Coincident(g100,g101)
    c: Coincident(g101,g102)
    c: Coincident(g102,g103)
    c: Coincident(g103,g104)
    c: Coincident(g104,g105)
    c: Coincident(g105,g106)
    c: Coincident(g106,g107)
    c: Coincident(g107,g108)
    c: Coincident(g108,g109)
    c: Coincident(g109,g110)
    c: Coincident(g110,g111)
    c: Coincident(g111,g112)
    c: Coincident(g112,g113)
    c: Coincident(g113,g114)
    c: Coincident(g114,g115)
    c: Coincident(g115,g116)
    c: Coincident(g116,g117)
    c: Coincident(g118,g119)
    c: Coincident(g119,g120)
    c: Coincident(g120,g121)
    c: Coincident(g121,g122)
    c: Coincident(g122,g123)
    c: Coincident(g123,g124)
    c: Coincident(g124,g125)
    c: Coincident(g125,g126)
    c: Coincident(g126,g127)
    c: Coincident(g127,g128)
    c: Coincident(g128,g129)
    c: Coincident(g129,g130)
    c: Coincident(g130,g131)
    c: Coincident(g131,g132)
    c: Coincident(g132,g133)
    c: Coincident(g133,g134)
    c: Coincident(g134,g135)
    c: Coincident(g135,g136)
    c: Symmetric(g69,g70,g-2)
    c: Symmetric(g51,g88,g-2)
    c: Symmetric(g50,g89,g-2)
    c: Symmetric(g32,g107,g-2)
    c: Symmetric(g31,g108,g-2)
    c: Symmetric(g13,g126,g-2)
    c: Symmetric(g12,g127,g-2)
    c: DistanceX(g13,g31) = 0.8
    c: DistanceX(g32,g50) = 0.8
    c: DistanceX(g51,g69) = 0.8
    c: DistanceX(g13,g13) = 9
    c: DistanceX(g32,g32) = 9
    c: DistanceX(g51,g51) = 9
    c: Horizontal(g139)
    c: Horizontal(g140)
    c: Horizontal(g141)
    c: Horizontal(g142)
    c: Horizontal(g143)
    c: Vertical(g8,g6)
    c: Vertical(g6,g4)
    c: Vertical(g144)
    c: Horizontal(g145)
    c: Coincident(g146,g0)
    c: Coincident(g146,g2)
    c: Coincident(g0,g137)
    c: Coincident(g2,g137)
    c: Horizontal(g147)
    c: PointOnObject(g11,g139)
    c: PointOnObject(g11,g144)
    c: PointOnObject(g10,g140)
    c: PointOnObject(g9,g144)
    c: PointOnObject(g7,g142)
    c: Horizontal(g138)
    c: DistanceY(g137,g147) = 4.5
    c: DistanceY(g147,g143) = 7
    c: DistanceY(g143,g138) = 7
    c: DistanceY(g138,g3) = 7
    c: DistanceY(g3,g140) = 7
    c: DistanceY(g140,g0) = 7
    c: Vertical(g139,g140)
    c: Vertical(g140,g141)
    c: Vertical(g141,g3)
    c: Vertical(g3,g142)
    c: Vertical(g142,g138)
    c: Vertical(g138,g145)
    c: Vertical(g145,g143)
    c: Vertical(g143,g147)
    c: DistanceY(g143,g145) = 2.4
    c: DistanceY(g138,g142) = 2.4
    c: DistanceY(g3,g141) = 2.4
    c: DistanceY(g140,g139) = 2.4
    c: Parallel(g12,g14)
    c: Parallel(g11,g15)
    c: PointOnObject(g14,g139)
    c: PointOnObject(g30,g139)
    c: PointOnObject(g15,g140)
    c: PointOnObject(g29,g140)
    c: Parallel(g14,g31)
    c: PointOnObject(g16,g141)
    c: PointOnObject(g28,g141)
    c: PointOnObject(g17,g3)
    c: PointOnObject(g27,g3)
    c: PointOnObject(g18,g142)
    c: PointOnObject(g26,g142)
    c: PointOnObject(g19,g138)
    c: PointOnObject(g25,g138)
    c: PointOnObject(g20,g145)
    c: PointOnObject(g24,g145)
    c: PointOnObject(g21,g143)
    c: PointOnObject(g23,g143)
    c: PointOnObject(g22,g147)
    c: PointOnObject(g23,g147)
    c: PointOnObject(g33,g139)
    c: PointOnObject(g49,g139)
    c: PointOnObject(g52,g139)
    c: PointOnObject(g71,g139)
    c: PointOnObject(g87,g139)
    c: PointOnObject(g90,g139)
    c: PointOnObject(g106,g139)
    c: PointOnObject(g109,g139)
    c: PointOnObject(g125,g139)
    c: PointOnObject(g128,g139)
    c: PointOnObject(g34,g140)
    c: PointOnObject(g48,g140)
    c: PointOnObject(g53,g140)
    c: PointOnObject(g67,g140)
    c: PointOnObject(g72,g140)
    c: PointOnObject(g86,g140)
    c: PointOnObject(g91,g140)
    c: PointOnObject(g105,g140)
    c: PointOnObject(g110,g140)
    c: PointOnObject(g124,g140)
    c: PointOnObject(g129,g140)
    c: Parallel(g33,g50)
    c: Parallel(g52,g69)
    c: Parallel(g71,g88)
    c: Parallel(g71,g90)
    c: Parallel(g90,g107)
    c: Parallel(g71,g109)
    c: Parallel(g109,g126)
    c: Parallel(g126,g128)
    c: Symmetric(g71,g68,g-2)
    c: Symmetric(g72,g67,g-2)
    c: Vertical(g139,g140)
    c: Vertical(g140,g141)
    c: Vertical(g141,g3)
    c: Vertical(g3,g142)
    c: Vertical(g142,g138)
    c: Vertical(g138,g145)
    c: Vertical(g145,g143)
    c: Vertical(g143,g147)
    c: Parallel(g34,g49)
    c: Parallel(g49,g53)
    c: Parallel(g53,g68)
    c: Parallel(g35,g48)
    c: Parallel(g48,g54)
    c: Parallel(g54,g67)
    c: PointOnObject(g35,g141)
    c: PointOnObject(g47,g141)
    c: PointOnObject(g54,g141)
    c: PointOnObject(g66,g141)
    c: PointOnObject(g85,g141)
    c: PointOnObject(g92,g141)
    c: PointOnObject(g104,g141)
    c: PointOnObject(g111,g141)
    c: PointOnObject(g123,g141)
    c: PointOnObject(g130,g141)
    c: Symmetric(g66,g73,g-2)
    c: Symmetric(g65,g74,g-2)
    c: PointOnObject(g36,g3)
    c: PointOnObject(g46,g3)
    c: PointOnObject(g55,g3)
    c: PointOnObject(g65,g3)
    c: Parallel(g36,g47)
    c: Parallel(g47,g55)
    c: Parallel(g55,g66)
    c: Symmetric(g64,g75,g-2)
    c: Symmetric(g79,g61,g-2)
    c: Symmetric(g61,g78,g-2)
    c: Symmetric(g62,g77,g-2)
    c: Symmetric(g63,g76,g-2)
    c: Parallel(g37,g46)
    c: Parallel(g46,g56)
    c: Parallel(g56,g65)
    c: PointOnObject(g37,g142)
    c: PointOnObject(g45,g142)
    c: PointOnObject(g56,g142)
    c: PointOnObject(g64,g142)
    c: PointOnObject(g38,g138)
    c: PointOnObject(g44,g138)
    c: PointOnObject(g57,g138)
    c: PointOnObject(g63,g138)
    c: Parallel(g38,g45)
    c: Parallel(g45,g57)
    c: Parallel(g57,g64)
    c: PointOnObject(g39,g145)
    c: PointOnObject(g43,g145)
    c: PointOnObject(g58,g145)
    c: PointOnObject(g62,g145)
    c: Parallel(g39,g44)
    c: Parallel(g44,g58)
    c: Parallel(g58,g63)
    c: Parallel(g40,g43)
    c: Parallel(g43,g59)
    c: Parallel(g59,g62)
    c: PointOnObject(g40,g143)
    c: PointOnObject(g42,g143)
    c: PointOnObject(g59,g143)
    c: PointOnObject(g61,g143)
    c: PointOnObject(g41,g147)
    c: PointOnObject(g42,g147)
    c: PointOnObject(g60,g147)
    c: PointOnObject(g61,g147)
    c: Parallel(g41,g42)
    c: Parallel(g42,g60)
    c: Parallel(g60,g61)
    c: PointOnObject(g80,g147)
    c: PointOnObject(g98,g147)
    c: PointOnObject(g99,g147)
    c: PointOnObject(g117,g147)
    c: PointOnObject(g118,g147)
    c: PointOnObject(g80,g143)
    c: PointOnObject(g97,g143)
    c: PointOnObject(g99,g143)
    c: PointOnObject(g116,g143)
    c: PointOnObject(g118,g143)
    c: PointOnObject(g135,g143)
    c: Parallel(g79,g80)
    c: Parallel(g80,g98)
    c: Parallel(g98,g99)
    c: Parallel(g99,g117)
    c: Parallel(g117,g118)
    c: Parallel(g118,g136)
    c: Parallel(g72,g87)
    c: Parallel(g87,g91)
    c: Parallel(g91,g106)
    c: Parallel(g106,g110)
    c: Parallel(g110,g125)
    c: Parallel(g125,g129)
    c: Parallel(g73,g86)
    c: Parallel(g86,g92)
    c: Parallel(g92,g105)
    c: Parallel(g105,g111)
    c: Parallel(g111,g124)
    c: Parallel(g124,g130)
    c: PointOnObject(g84,g3)
    c: PointOnObject(g93,g3)
    c: PointOnObject(g103,g3)
    c: PointOnObject(g112,g3)
    c: PointOnObject(g122,g3)
    c: PointOnObject(g131,g3)
    c: Parallel(g74,g85)
    c: Parallel(g85,g93)
    c: Parallel(g93,g104)
    c: Parallel(g104,g112)
    c: Parallel(g112,g123)
    c: Parallel(g123,g131)
    c: PointOnObject(g83,g142)
    c: PointOnObject(g94,g142)
    c: PointOnObject(g102,g142)
    c: PointOnObject(g113,g142)
    c: PointOnObject(g121,g142)
    c: PointOnObject(g132,g142)
    c: Parallel(g75,g84)
    c: Parallel(g84,g94)
    c: Parallel(g94,g103)
    c: Parallel(g103,g113)
    c: Parallel(g113,g122)
    c: Parallel(g122,g132)
    c: PointOnObject(g82,g138)
    c: PointOnObject(g95,g138)
    c: PointOnObject(g101,g138)
    c: PointOnObject(g114,g138)
    c: PointOnObject(g120,g138)
    c: PointOnObject(g133,g138)
    c: PointOnObject(g81,g145)
    c: PointOnObject(g96,g145)
    c: PointOnObject(g100,g145)
    c: PointOnObject(g115,g145)
    c: PointOnObject(g119,g145)
    c: PointOnObject(g134,g145)
    c: Parallel(g76,g83)
    c: Parallel(g83,g95)
    c: Parallel(g95,g102)
    c: Parallel(g102,g114)
    c: Parallel(g114,g121)
    c: Parallel(g121,g133)
    c: Parallel(g77,g82)
    c: Parallel(g82,g96)
    c: Parallel(g96,g101)
    c: Parallel(g101,g115)
    c: Parallel(g115,g120)
    c: Parallel(g120,g134)
    c: Parallel(g78,g81)
    c: Parallel(g81,g97)
    c: Parallel(g97,g100)
    c: Parallel(g100,g116)
    c: Parallel(g116,g119)
    c: Parallel(g119,g135)
    c: DistanceY(g137,g-1) = 0
    c: PointOnObject(g148,g154)
    c: PointOnObject(g149,g154)
    c: PointOnObject(g150,g154)
    c: PointOnObject(g151,g154)
    c: PointOnObject(g152,g154)
    c: PointOnObject(g153,g154)
    c: PointOnObject(g22,g148)
    c: PointOnObject(g23,g148)
    c: PointOnObject(g41,g149)
    c: PointOnObject(g42,g149)
    c: PointOnObject(g60,g150)
    c: PointOnObject(g61,g150)
    c: PointOnObject(g79,g151)
    c: PointOnObject(g98,g152)
    c: PointOnObject(g99,g152)
    c: PointOnObject(g117,g153)
    c: PointOnObject(g118,g153)
    c: PointOnObject(g153,g147)
    c: PointOnObject(g153,g147)
    c: PointOnObject(g152,g147)
    c: PointOnObject(g152,g147)
    c: PointOnObject(g151,g147)
    c: PointOnObject(g151,g147)
    c: PointOnObject(g150,g147)
    c: PointOnObject(g150,g147)
    c: PointOnObject(g149,g147)
    c: PointOnObject(g149,g147)
    c: PointOnObject(g148,g147)
    c: PointOnObject(g148,g147)
    c: DistanceY(g154,g147) = 1.5
    c: Vertical(g147,g154)
    c: Vertical(g147,g154)
    c: Coincident(g136,g137)
    c: Coincident(g4,g137)
    c: Coincident(g0,g12)
    c: PointOnObject(g31,g1)
    c: PointOnObject(g50,g1)
    c: PointOnObject(g69,g1)
    c: PointOnObject(g6,g0)
    c: DistanceX(g144,g12) = 0.4
    c: PointOnObject(g9,g141)
    c: PointOnObject(g8,g3)
    c: PointOnObject(g7,g144)
    c: PointOnObject(g6,g138)
    c: PointOnObject(g5,g145)
    c: PointOnObject(g5,g144)
    c: PointOnObject(g4,g143)
    c: Parallel(g12,g33)
    c: Parallel(g12,g52)
    c: Parallel(g15,g30)
    c: Parallel(g11,g34)
    c: PointOnObject(g10,g0)
    c: Parallel(g16,g29)
    c: Parallel(g10,g16)
    c: Parallel(g10,g35)
    c: Parallel(g9,g17)
    c: Parallel(g17,g28)
    c: Parallel(g9,g36)
    c: Parallel(g18,g27)
    c: Parallel(g8,g18)
    c: Parallel(g8,g37)
    c: Parallel(g7,g19)
    c: Parallel(g19,g26)
    c: Parallel(g6,g20)
    c: Parallel(g20,g25)
    c: Parallel(g7,g38)
    c: Parallel(g6,g39)
    c: Symmetric(g150,g151,g-2)
    c: DistanceX(g150,g151) = 9.8
    c: Parallel(g23,g22)
    c: Parallel(g21,g24)
    c: Parallel(g5,g21)
    c: Parallel(g41,g23)
FEATURE [PartDesign::Pad] Pad  label="FixatorPadBody"
  Direction = (0,0,1)
  Length = 6
  Length2 = 10
  Profile = -> Sketch022
  ReferenceAxis = -> Sketch022 [N_Axis]
  Type = 0
  expr: Length = Spreadsheet.mmCellHight
FEATURE [Sketcher::SketchObject] Sketch  label="PiercesPocketSketch"
  AttachmentOffset = pos=(0,0,0) rot=(1,0,0;1.5708rad)
  FullyConstrained = true
  MapMode = 2
  Placement = pos=(0,0,0) rot=(0.707107,0.707107,0;3.14159rad)
  Support = -> [YZ_Plane005]
  expr: Constraints[108] = Spreadsheet.mmCellPierceWidth
  expr: Constraints[118] = Spreadsheet.mmCellPierceWidth
  expr: Constraints[128] = Spreadsheet.mmCellPierceWidth
  expr: Constraints[138] = Spreadsheet.mmCellPierceWidth
  expr: Constraints[148] = Spreadsheet.mmCellPierceWidth
  expr: Constraints[158] = Spreadsheet.mmCellPierceWidth
  expr: Constraints[171] = Spreadsheet.mmCellWidth + Spreadsheet.mmCellWall
  expr: Constraints[172] = Spreadsheet.mmCellWidth + Spreadsheet.mmCellWall
  expr: Constraints[173] = Spreadsheet.mmCellWidth + Spreadsheet.mmCellWall
  expr: Constraints[174] = Spreadsheet.mmCellWidth + Spreadsheet.mmCellWall
  expr: Constraints[175] = Spreadsheet.mmCellWidth + Spreadsheet.mmCellWall
  expr: Constraints[176] = Spreadsheet.mmCellWidth + Spreadsheet.mmCellWall
  expr: Constraints[178] = Spreadsheet.mmCellWidth / 2
  expr: Constraints[179] = Spreadsheet.mmCellWidth / 2
  expr: Constraints[180] = Spreadsheet.mmCommonBaseLenght + Spreadsheet.mmToothStep * 1.5
  expr: Constraints[181] = Spreadsheet.mmToothStep * 2
  expr: Constraints[19] = Spreadsheet.mmCellPierceWidth
  expr: Constraints[29] = Spreadsheet.mmCellPierceWidth
  expr: Constraints[39] = Spreadsheet.mmCellPierceWidth
  expr: Constraints[49] = Spreadsheet.mmCellPierceWidth
  expr: Constraints[59] = Spreadsheet.mmCellPierceWidth
  expr: Constraints[69] = Spreadsheet.mmCellPierceWidth
  expr: Constraints[82] = Spreadsheet.mmCellWidth + Spreadsheet.mmCellWall
  expr: Constraints[83] = Spreadsheet.mmCellWidth + Spreadsheet.mmCellWall
  expr: Constraints[84] = Spreadsheet.mmCellWidth + Spreadsheet.mmCellWall
  expr: Constraints[85] = Spreadsheet.mmCellWidth + Spreadsheet.mmCellWall
  expr: Constraints[86] = Spreadsheet.mmCellWidth + Spreadsheet.mmCellWall
  expr: Constraints[87] = Spreadsheet.mmCellWidth + Spreadsheet.mmCellWall
  expr: Constraints[98] = Spreadsheet.mmCellPierceWidth
  expr: Constraints[9] = Spreadsheet.mmCellPierceWidth
  sketch-geometry (56):
    g0: ArcOfCircle CenterX=29 CenterY=0 CenterZ=0 NormalX=0 NormalY=0 NormalZ=1 AngleXU=0 Radius=3.0104 StartAngle=2.41495 EndAngle=3.86823
    g1: LineSegment StartX=26.75 StartY=2 StartZ=0 EndX=31.25 EndY=2 EndZ=0
    g2: LineSegment StartX=26.75 StartY=-2 StartZ=0 EndX=31.25 EndY=-2 EndZ=0
    g3: ArcOfCircle CenterX=29 CenterY=0 CenterZ=0 NormalX=0 NormalY=0 NormalZ=1 AngleXU=0 Radius=3.0104 StartAngle=5.55654 EndAngle=7.00983
    g4: ArcOfCircle CenterX=29 CenterY=9.8 CenterZ=0 NormalX=0 NormalY=0 NormalZ=1 AngleXU=0 Radius=3.0104 StartAngle=2.41495 EndAngle=3.86823
    g5: LineSegment StartX=26.75 StartY=11.8 StartZ=0 EndX=31.25 EndY=11.8 EndZ=0
    g6: LineSegment StartX=26.75 StartY=7.8 StartZ=0 EndX=31.25 EndY=7.8 EndZ=0
    g7: ArcOfCircle CenterX=29 CenterY=9.8 CenterZ=0 NormalX=0 NormalY=0 NormalZ=1 AngleXU=0 Radius=3.0104 StartAngle=5.55654 EndAngle=7.00983
    g8: ArcOfCircle CenterX=29 CenterY=19.6 CenterZ=0 NormalX=0 NormalY=0 NormalZ=1 AngleXU=0 Radius=3.0104 StartAngle=2.41495 EndAngle=3.86823
    g9: LineSegment StartX=26.75 StartY=21.6 StartZ=0 EndX=31.25 EndY=21.6 EndZ=0
    g10: LineSegment StartX=26.75 StartY=17.6 StartZ=0 EndX=31.25 EndY=17.6 EndZ=0
    g11: ArcOfCircle CenterX=29 CenterY=19.6 CenterZ=0 NormalX=0 NormalY=0 NormalZ=1 AngleXU=0 Radius=3.0104 StartAngle=5.55654 EndAngle=7.00983
    g12: ArcOfCircle CenterX=29 CenterY=29.4 CenterZ=0 NormalX=0 NormalY=0 NormalZ=1 AngleXU=0 Radius=3.0104 StartAngle=2.41495 EndAngle=3.86823
    g13: LineSegment StartX=26.75 StartY=31.4 StartZ=0 EndX=31.25 EndY=31.4 EndZ=0
    g14: LineSegment StartX=26.75 StartY=27.4 StartZ=0 EndX=31.25 EndY=27.4 EndZ=0
    g15: ArcOfCircle CenterX=29 CenterY=29.4 CenterZ=0 NormalX=0 NormalY=0 NormalZ=1 AngleXU=0 Radius=3.0104 StartAngle=5.55654 EndAngle=7.00983
    g16: ArcOfCircle CenterX=29 CenterY=-9.8 CenterZ=0 NormalX=0 NormalY=0 NormalZ=1 AngleXU=0 Radius=3.0104 StartAngle=2.41495 EndAngle=3.86823
    g17: LineSegment StartX=26.75 StartY=-7.8 StartZ=0 EndX=31.25 EndY=-7.8 EndZ=0
    g18: LineSegment StartX=26.75 StartY=-11.8 StartZ=0 EndX=31.25 EndY=-11.8 EndZ=0
    g19: ArcOfCircle CenterX=29 CenterY=-9.8 CenterZ=0 NormalX=0 NormalY=0 NormalZ=1 AngleXU=0 Radius=3.0104 StartAngle=5.55654 EndAngle=7.00983
    g20: ArcOfCircle CenterX=29 CenterY=-19.6 CenterZ=0 NormalX=0 NormalY=0 NormalZ=1 AngleXU=0 Radius=3.0104 StartAngle=2.41495 EndAngle=3.86823
    g21: LineSegment StartX=26.75 StartY=-17.6 StartZ=0 EndX=31.25 EndY=-17.6 EndZ=0
    g22: LineSegment StartX=26.75 StartY=-21.6 StartZ=0 EndX=31.25 EndY=-21.6 EndZ=0
    g23: ArcOfCircle CenterX=29 CenterY=-19.6 CenterZ=0 NormalX=0 NormalY=0 NormalZ=1 AngleXU=0 Radius=3.0104 StartAngle=5.55654 EndAngle=7.00983
    g24: ArcOfCircle CenterX=29 CenterY=-29.4 CenterZ=0 NormalX=0 NormalY=0 NormalZ=1 AngleXU=0 Radius=3.0104 StartAngle=2.41495 EndAngle=3.86823
    g25: LineSegment StartX=26.75 StartY=-27.4 StartZ=0 EndX=31.25 EndY=-27.4 EndZ=0
    g26: LineSegment StartX=26.75 StartY=-31.4 StartZ=0 EndX=31.25 EndY=-31.4 EndZ=0
    g27: ArcOfCircle CenterX=29 CenterY=-29.4 CenterZ=0 NormalX=0 NormalY=0 NormalZ=1 AngleXU=0 Radius=3.0104 StartAngle=5.55654 EndAngle=7.00983
    g28: ArcOfCircle CenterX=15 CenterY=0 CenterZ=0 NormalX=0 NormalY=0 NormalZ=1 AngleXU=0 Radius=3.0104 StartAngle=2.41495 EndAngle=3.86823
    g29: LineSegment StartX=12.75 StartY=2 StartZ=0 EndX=17.25 EndY=2 EndZ=0
    g30: LineSegment StartX=12.75 StartY=-2 StartZ=0 EndX=17.25 EndY=-2 EndZ=0
    g31: ArcOfCircle CenterX=15 CenterY=0 CenterZ=0 NormalX=0 NormalY=0 NormalZ=1 AngleXU=0 Radius=3.0104 StartAngle=5.55654 EndAngle=7.00983
    g32: ArcOfCircle CenterX=15 CenterY=9.8 CenterZ=0 NormalX=0 NormalY=0 NormalZ=1 AngleXU=0 Radius=3.0104 StartAngle=2.41495 EndAngle=3.86823
    g33: LineSegment StartX=12.75 StartY=11.8 StartZ=0 EndX=17.25 EndY=11.8 EndZ=0
    g34: LineSegment StartX=12.75 StartY=7.8 StartZ=0 EndX=17.25 EndY=7.8 EndZ=0
    g35: ArcOfCircle CenterX=15 CenterY=9.8 CenterZ=0 NormalX=0 NormalY=0 NormalZ=1 AngleXU=0 Radius=3.0104 StartAngle=5.55654 EndAngle=7.00983
    g36: ArcOfCircle CenterX=15 CenterY=19.6 CenterZ=0 NormalX=0 NormalY=0 NormalZ=1 AngleXU=0 Radius=3.0104 StartAngle=2.41495 EndAngle=3.86823
    g37: LineSegment StartX=12.75 StartY=21.6 StartZ=0 EndX=17.25 EndY=21.6 EndZ=0
    g38: LineSegment StartX=12.75 StartY=17.6 StartZ=0 EndX=17.25 EndY=17.6 EndZ=0
    g39: ArcOfCircle CenterX=15 CenterY=19.6 CenterZ=0 NormalX=0 NormalY=0 NormalZ=1 AngleXU=0 Radius=3.0104 StartAngle=5.55654 EndAngle=7.00983
    g40: ArcOfCircle CenterX=15 CenterY=29.4 CenterZ=0 NormalX=0 NormalY=0 NormalZ=1 AngleXU=0 Radius=3.0104 StartAngle=2.41495 EndAngle=3.86823
    g41: LineSegment StartX=12.75 StartY=31.4 StartZ=0 EndX=17.25 EndY=31.4 EndZ=0
    g42: LineSegment StartX=12.75 StartY=27.4 StartZ=0 EndX=17.25 EndY=27.4 EndZ=0
    g43: ArcOfCircle CenterX=15 CenterY=29.4 CenterZ=0 NormalX=0 NormalY=0 NormalZ=1 AngleXU=0 Radius=3.0104 StartAngle=5.55654 EndAngle=7.00983
    g44: ArcOfCircle CenterX=15 CenterY=-9.8 CenterZ=0 NormalX=0 NormalY=0 NormalZ=1 AngleXU=0 Radius=3.0104 StartAngle=2.41495 EndAngle=3.86823
    g45: LineSegment StartX=12.75 StartY=-7.8 StartZ=0 EndX=17.25 EndY=-7.8 EndZ=0
    g46: LineSegment StartX=12.75 StartY=-11.8 StartZ=0 EndX=17.25 EndY=-11.8 EndZ=0
    g47: ArcOfCircle CenterX=15 CenterY=-9.8 CenterZ=0 NormalX=0 NormalY=0 NormalZ=1 AngleXU=0 Radius=3.0104 StartAngle=5.55654 EndAngle=7.00983
    g48: ArcOfCircle CenterX=15 CenterY=-19.6 CenterZ=0 NormalX=0 NormalY=0 NormalZ=1 AngleXU=0 Radius=3.0104 StartAngle=2.41495 EndAngle=3.86823
    g49: LineSegment StartX=12.75 StartY=-17.6 StartZ=0 EndX=17.25 EndY=-17.6 EndZ=0
    g50: LineSegment StartX=12.75 StartY=-21.6 StartZ=0 EndX=17.25 EndY=-21.6 EndZ=0
    g51: ArcOfCircle CenterX=15 CenterY=-19.6 CenterZ=0 NormalX=0 NormalY=0 NormalZ=1 AngleXU=0 Radius=3.0104 StartAngle=5.55654 EndAngle=7.00983
    g52: ArcOfCircle CenterX=15 CenterY=-29.4 CenterZ=0 NormalX=0 NormalY=0 NormalZ=1 AngleXU=0 Radius=3.0104 StartAngle=2.41495 EndAngle=3.86823
    g53: LineSegment StartX=12.75 StartY=-27.4 StartZ=0 EndX=17.25 EndY=-27.4 EndZ=0
    g54: LineSegment StartX=12.75 StartY=-31.4 StartZ=0 EndX=17.25 EndY=-31.4 EndZ=0
    g55: ArcOfCircle CenterX=15 CenterY=-29.4 CenterZ=0 NormalX=0 NormalY=0 NormalZ=1 AngleXU=0 Radius=3.0104 StartAngle=5.55654 EndAngle=7.00983
  constraints (182):
    c: Horizontal(g1)
    c: Horizontal(g2)
    c: PointOnObject(g1,g0)
    c: Coincident(g0,g3)
    c: Coincident(g0,g2)
    c: Coincident(g3,g2)
    c: Coincident(g1,g0)
    c: Coincident(g3,g1)
    c: Equal(g2,g1)
    c: DistanceY(g2,g1) = 4
    c: Horizontal(g5)
    c: Horizontal(g6)
    c: PointOnObject(g5,g4)
    c: Coincident(g4,g7)
    c: Coincident(g4,g6)
    c: Coincident(g7,g6)
    c: Coincident(g5,g4)
    c: Coincident(g7,g5)
    c: Equal(g6,g5)
    c: DistanceY(g6,g5) = 4
    c: Horizontal(g9)
    c: Horizontal(g10)
    c: PointOnObject(g9,g8)
    c: Coincident(g8,g11)
    c: Coincident(g8,g10)
    c: Coincident(g11,g10)
    c: Coincident(g9,g8)
    c: Coincident(g11,g9)
    c: Equal(g10,g9)
    c: DistanceY(g10,g9) = 4
    c: Horizontal(g13)
    c: Horizontal(g14)
    c: PointOnObject(g13,g12)
    c: Coincident(g12,g15)
    c: Coincident(g12,g14)
    c: Coincident(g15,g14)
    c: Coincident(g13,g12)
    c: Coincident(g15,g13)
    c: Equal(g14,g13)
    c: DistanceY(g14,g13) = 4
    c: Horizontal(g17)
    c: Horizontal(g18)
    c: PointOnObject(g17,g16)
    c: Coincident(g16,g19)
    c: Coincident(g16,g18)
    c: Coincident(g19,g18)
    c: Coincident(g17,g16)
    c: Coincident(g19,g17)
    c: Equal(g18,g17)
    c: DistanceY(g18,g17) = 4
    c: Horizontal(g21)
    c: Horizontal(g22)
    c: PointOnObject(g21,g20)
    c: Coincident(g20,g23)
    c: Coincident(g20,g22)
    c: Coincident(g23,g22)
    c: Coincident(g21,g20)
    c: Coincident(g23,g21)
    c: Equal(g22,g21)
    c: DistanceY(g22,g21) = 4
    c: Horizontal(g25)
    c: Horizontal(g26)
    c: PointOnObject(g25,g24)
    c: Coincident(g24,g27)
    c: Coincident(g24,g26)
    c: Coincident(g27,g26)
    c: Coincident(g25,g24)
    c: Coincident(g27,g25)
    c: Equal(g26,g25)
    c: DistanceY(g26,g25) = 4
    c: Vertical(g0,g4)
    c: Vertical(g4,g8)
    c: Vertical(g8,g12)
    c: Vertical(g12,g16)
    c: Vertical(g16,g20)
    c: Vertical(g20,g24)
    c: Equal(g2,g18)
    c: Equal(g18,g22)
    c: Equal(g22,g26)
    c: Equal(g1,g5)
    c: Equal(g5,g9)
    c: Equal(g9,g13)
    c: DistanceY(g8,g12) = 9.8
    c: DistanceY(g4,g8) = 9.8
    c: DistanceY(g0,g4) = 9.8
    c: DistanceY(g16,g0) = 9.8
    c: DistanceY(g20,g16) = 9.8
    c: DistanceY(g24,g20) = 9.8
    c: PointOnObject(g0,g-1)
    c: Horizontal(g29)
    c: Horizontal(g30)
    c: PointOnObject(g29,g28)
    c: Coincident(g28,g31)
    c: Coincident(g28,g30)
    c: Coincident(g31,g30)
    c: Coincident(g29,g28)
    c: Coincident(g31,g29)
    c: Equal(g30,g29)
    c: DistanceY(g30,g29) = 4
    c: Horizontal(g33)
    c: Horizontal(g34)
    c: PointOnObject(g33,g32)
    c: Coincident(g32,g35)
    c: Coincident(g32,g34)
    c: Coincident(g35,g34)
    c: Coincident(g33,g32)
    c: Coincident(g35,g33)
    c: Equal(g34,g33)
    c: DistanceY(g34,g33) = 4
    c: Horizontal(g37)
    c: Horizontal(g38)
    c: PointOnObject(g37,g36)
    c: Coincident(g36,g39)
    c: Coincident(g36,g38)
    c: Coincident(g39,g38)
    c: Coincident(g37,g36)
    c: Coincident(g39,g37)
    c: Equal(g38,g37)
    c: DistanceY(g38,g37) = 4
    c: Horizontal(g41)
    c: Horizontal(g42)
    c: PointOnObject(g41,g40)
    c: Coincident(g40,g43)
    c: Coincident(g40,g42)
    c: Coincident(g43,g42)
    c: Coincident(g41,g40)
    c: Coincident(g43,g41)
    c: Equal(g42,g41)
    c: DistanceY(g42,g41) = 4
    c: Horizontal(g45)
    c: Horizontal(g46)
    c: PointOnObject(g45,g44)
    c: Coincident(g44,g47)
    c: Coincident(g44,g46)
    c: Coincident(g47,g46)
    c: Coincident(g45,g44)
    c: Coincident(g47,g45)
    c: Equal(g46,g45)
    c: DistanceY(g46,g45) = 4
    c: Horizontal(g49)
    c: Horizontal(g50)
    c: PointOnObject(g49,g48)
    c: Coincident(g48,g51)
    c: Coincident(g48,g50)
    c: Coincident(g51,g50)
    c: Coincident(g49,g48)
    c: Coincident(g51,g49)
    c: Equal(g50,g49)
    c: DistanceY(g50,g49) = 4
    c: Horizontal(g53)
    c: Horizontal(g54)
    c: PointOnObject(g53,g52)
    c: Coincident(g52,g55)
    c: Coincident(g52,g54)
    c: Coincident(g55,g54)
    c: Coincident(g53,g52)
    c: Coincident(g55,g53)
    c: Equal(g54,g53)
    c: DistanceY(g54,g53) = 4
    c: Vertical(g28,g32)
    c: Vertical(g32,g36)
    c: Vertical(g36,g40)
    c: Vertical(g40,g44)
    c: Vertical(g44,g48)
    c: Vertical(g48,g52)
    c: Equal(g30,g46)
    c: Equal(g46,g50)
    c: Equal(g50,g54)
    c: Equal(g29,g33)
    c: Equal(g33,g37)
    c: Equal(g37,g41)
    c: DistanceY(g36,g40) = 9.8
    c: DistanceY(g32,g36) = 9.8
    c: DistanceY(g28,g32) = 9.8
    c: DistanceY(g44,g28) = 9.8
    c: DistanceY(g48,g44) = 9.8
    c: DistanceY(g52,g48) = 9.8
    c: PointOnObject(g28,g-1)
    c: DistanceX(g24,g26) = 4.5
    c: DistanceX(g52,g54) = 4.5
    c: DistanceX(g-1,g28) = 15
    c: DistanceX(g28,g0) = 14
FEATURE [PartDesign::Pocket] Pocket  label="PiercesPocket"
  BaseFeature = -> Pad
  Direction = (-2e-16,2e-16,1)
  Length = 69.4
  Length2 = 5
  Midplane = true
  Profile = -> Sketch
  ReferenceAxis = -> Sketch [N_Axis]
  Type = 0
  expr: Length = Spreadsheet.mmBaseWidth + Spreadsheet.mmCellWall * 2
FEATURE [PartDesign::Body] Body004  label="BeamFixator"
  Group = -> [Sketch022,Pad,Sketch,Pocket]
  Origin = -> Origin005
  Tip = -> Pocket
COMPONENT P3 — recipe-attached ("HingePart", modeled in this document).
Construction recipe (the document's own serialized feature program — sketch geometry with constraints, then the solid features built on it; lengths are millimeters unless a unit is written):

FEATURE [PartDesign::LinearPattern] LinearPattern
  Direction = -> Sketch007 [V_Axis]
  Length = 67.8
  Occurrences = 4
  Originals = -> [Revolution,Revolution004,Pocket001,Pocket002,Pad008,Pad009,Pad010,Pad011,Pocket004,Pocket005]
  expr: Length = Spreadsheet.mmHingeHight
  expr: Occurrences = Spreadsheet.nHingeHightDiskCnt
FEATURE [PartDesign::Body] Body005
  Group = -> [LinearPattern]
  Origin = -> Origin007
  Tip = -> LinearPattern
COMPONENT P4 — recipe-attached ("AxisFixatorPart", modeled in this document).
Construction recipe (the document's own serialized feature program — sketch geometry with constraints, then the solid features built on it; lengths are millimeters unless a unit is written):

FEATURE [Sketcher::SketchObject] Sketch027  label="CommonFixatorScatch"
  FullyConstrained = false
  MapMode = 5
  Placement = pos=(0,0,0) rot=(0.57735,0.57735,0.57735;2.0944rad)
  Support = -> [YZ_Plane013]
  expr: Constraints[0] = Spreadsheet.mmAxisTubeDia + 2 * Spreadsheet.mmFixatorThick + 2 * Spreadsheet.mmTwoSideTapeThick
  expr: Constraints[17] = Spreadsheet.mmAxisTubeDia / 2 + Spreadsheet.mmPetalHightMax + Spreadsheet.mmTwoSideTapeThick
  expr: Constraints[18] = Spreadsheet.mmAxisTubeDia / 2 + Spreadsheet.mmPetalHightMax + Spreadsheet.mmTwoSideTapeThick
  expr: Constraints[32] = Spreadsheet.mmPetalPocketWidth
  expr: Constraints[33] = Spreadsheet.mmBaseWidth
  expr: Constraints[3] = Spreadsheet.mmAxisTubeDia
  sketch-geometry (14):
    g0: Circle CenterX=0 CenterY=0 CenterZ=0 NormalX=0 NormalY=0 NormalZ=1 AngleXU=0 Radius=26.72
    g1: LineSegment StartX=0 StartY=0 StartZ=0 EndX=32.2586 EndY=18.6245 EndZ=0
    g2: ArcOfCircle CenterX=0 CenterY=0 CenterZ=0 NormalX=0 NormalY=0 NormalZ=1 AngleXU=0 Radius=20.4 StartAngle=5.32461 EndAngle=6.86682
    g3: LineSegment StartX=0 StartY=-20.4 StartZ=0 EndX=0 EndY=-39.1443 EndZ=0
    g4: LineSegment StartX=0 StartY=-39.1443 StartZ=0 EndX=6.1902 EndY=-42.7183 EndZ=0
    g5: LineSegment StartX=6.1902 StartY=-42.7183 StartZ=0 EndX=40.0902 EndY=15.9983 EndZ=0
    g6: LineSegment StartX=40.0902 StartY=15.9983 StartZ=0 EndX=33.9 EndY=19.5722 EndZ=0
    g7: LineSegment StartX=33.9 StartY=19.5722 StartZ=0 EndX=17.6669 EndY=10.2 EndZ=0
    g8: LineSegment StartX=14.7156 StartY=-14.1284 StartZ=0 EndX=17.9224 EndY=-19.6828 EndZ=0
    g9: LineSegment StartX=17.9224 StartY=-19.6828 StartZ=0 EndX=8.08455 EndY=-25.3627 EndZ=0
    g10: LineSegment StartX=8.08455 StartY=-25.3627 StartZ=0 EndX=4.87772 EndY=-19.8083 EndZ=0
    g11: ArcOfCircle CenterX=0 CenterY=0 CenterZ=0 NormalX=0 NormalY=0 NormalZ=1 AngleXU=0 Radius=20.4 StartAngle=4.71239 EndAngle=4.95383
    g12: ArcOfCircle CenterX=0 CenterY=0 CenterZ=0 NormalX=0 NormalY=0 NormalZ=1 AngleXU=0 Radius=20.4 StartAngle=5.51814 EndAngle=6.80678
    g13: LineSegment StartX=0 StartY=0 StartZ=0 EndX=18.7992 EndY=-32.5612 EndZ=0
  constraints (39):
    c: Diameter(g0) = 53.44
    c: Angle(g-1,g1) = 0.523599
    c: PointOnObject(g6,g1)
    c: Diameter(g2) = 40.8
    c: Vertical(g3)
    c: Coincident(g3,g4)
    c: Coincident(g4,g5)
    c: Coincident(g5,g6)
    c: Coincident(g6,g7)
    c: Coincident(g8,g9)
    c: Coincident(g9,g10)
    c: Equal(g2,g11)
    c: Coincident(g2,g11)
    c: PointOnObject(g3,g-2)
    c: Parallel(g4,g6)
    c: Perpendicular(g5,g4)
    c: Tangent(g0,g5)
    c: Distance(g8,g11) = 26.62
    c: Distance(g9,g11) = 26.62
    c: Coincident(g11,g12)
    c: PointOnObject(g7,g1)
    c: Coincident(g10,g11)
    c: Coincident(g11,g3)
    c: Coincident(g12,g8)
    c: PointOnObject(g12,g1)
    c: Coincident(g12,g7)
    c: PointOnObject(g7,g1)
    c: Perpendicular(g10,g9)
    c: Perpendicular(g9,g8)
    c: Coincident(g13,g11)
    c: Angle(g13,g-1) = 1.0472
    c: Symmetric(g10,g8,g13)
    c: Distance(g10,g8) = 11.3598
    c: Distance(g4,g5) = 67.8
    c: Equal(g4,g6)
    c: Equal(g3,g7)
    c: Coincident(g-1,g0)
    c: Coincident(g0,g11)
    c: Coincident(g11,g1)
FEATURE [PartDesign::Pad] Pad012  label="AxisFixatorBodyPad"
  Direction = (1,-2e-16,3e-16)
  Length = 20.4
  Length2 = 10
  Placement = pos=(0,0,0) rot=(0.57735,0.57735,0.57735;2.0944rad)
  Profile = -> Sketch027
  ReferenceAxis = -> Sketch027 [N_Axis]
  Type = 0
  expr: Length = Spreadsheet.mmFixatorHight
FEATURE [Sketcher::SketchObject] Sketch031  label="MaxPetalBase001"
  FullyConstrained = false
  MapMode = 5
  Placement = pos=(0,0,0) rot=(0.57735,0.57735,0.57735;2.0944rad)
  Support = -> [YZ_Plane013]
  expr: Constraints[0] = Spreadsheet.mmAxisTubeDia + 2 * Spreadsheet.mmFixatorThick
  expr: Constraints[10] = Spreadsheet.mmAxisTubeDia
  expr: Constraints[12] = Spreadsheet.mmPetalPocketWidth
  expr: Constraints[1] = Spreadsheet.mmAxisTubeDia
  expr: Constraints[6] = Spreadsheet.mmAxisTubeDia / 2 + Spreadsheet.mmPetalHightMax
  sketch-geometry (7):
    g0: Circle CenterX=0 CenterY=2.5e-15 CenterZ=0 NormalX=0 NormalY=0 NormalZ=1 AngleXU=0 Radius=39.855
    g1: Circle CenterX=0 CenterY=2.5e-15 CenterZ=0 NormalX=0 NormalY=0 NormalZ=1 AngleXU=0 Radius=26.62
    g2: ArcOfCircle CenterX=0 CenterY=2.5e-15 CenterZ=0 NormalX=0 NormalY=0 NormalZ=1 AngleXU=0 Radius=20.4 StartAngle=5.86056 EndAngle=6.76902
    g3: LineSegment StartX=19.5933 StartY=5.67991 StartZ=0 EndX=26.52 EndY=5.67991 EndZ=0
    g4: LineSegment StartX=26.52 StartY=5.67991 StartZ=0 EndX=26.52 EndY=-5.67991 EndZ=0
    g5: LineSegment StartX=26.52 StartY=-5.67991 StartZ=0 EndX=19.5933 EndY=-5.67991 EndZ=0
    g6: ArcOfCircle CenterX=0 CenterY=2.5e-15 CenterZ=0 NormalX=0 NormalY=0 NormalZ=1 AngleXU=0 Radius=20.4 StartAngle=6.00103 EndAngle=6.56534
  constraints (17):
    c: Diameter(g1) = 53.24
    c: Diameter(g2) = 40.8
    c: Coincident(g3,g4)
    c: Coincident(g4,g5)
    c: Coincident(g0,g2)
    c: Vertical(g4)
    c: DistanceX(g-1,g4) = 26.52
    c: Coincident(g6,g0)
    c: Coincident(g6,g3)
    c: Coincident(g6,g5)
    c: Diameter(g6) = 40.8
    c: Symmetric(g3,g5,g-1)
    c: DistanceY(g5,g3) = 11.3598
    c: Horizontal(g3)
    c: Horizontal(g5)
    c: Coincident(g1,g6)
    c: Coincident(g-1,g6)
FEATURE [Sketcher::SketchObject] Sketch032  label="MinPetalBase001"
  AttachmentOffset = pos=(0,0,18.36) rot=(0,0,1;0rad)
  FullyConstrained = false
  MapMode = 5
  Placement = pos=(18.36,-4.1e-15,4.1e-15) rot=(0.57735,0.57735,0.57735;2.0944rad)
  Support = -> [YZ_Plane013]
  expr: .AttachmentOffset.Base.z = Spreadsheet.mmFixatorHight * 0.9
  expr: Constraints[0] = Spreadsheet.mmAxisTubeDia + 2 * Spreadsheet.mmFixatorThick
  expr: Constraints[10] = Spreadsheet.mmAxisTubeDia
  expr: Constraints[12] = Spreadsheet.mmPetalPocketWidth
  expr: Constraints[1] = Spreadsheet.mmAxisTubeDia
  expr: Constraints[6] = Spreadsheet.mmAxisTubeDia / 2 + Spreadsheet.mmPetalHightMin
  sketch-geometry (7):
    g0: Circle CenterX=0 CenterY=2e-15 CenterZ=0 NormalX=0 NormalY=0 NormalZ=1 AngleXU=0 Radius=39.844
    g1: Circle CenterX=0 CenterY=2e-15 CenterZ=0 NormalX=0 NormalY=0 NormalZ=1 AngleXU=0 Radius=26.62
    g2: ArcOfCircle CenterX=0 CenterY=2e-15 CenterZ=0 NormalX=0 NormalY=0 NormalZ=1 AngleXU=0 Radius=20.4 StartAngle=3.89517 EndAngle=6.7757
    g3: LineSegment StartX=19.5933 StartY=5.67991 StartZ=0 EndX=23.46 EndY=5.67991 EndZ=0
    g4: LineSegment StartX=23.46 StartY=5.67991 StartZ=0 EndX=23.46 EndY=-5.67991 EndZ=0
    g5: LineSegment StartX=23.46 StartY=-5.67991 StartZ=0 EndX=19.5933 EndY=-5.67991 EndZ=0
    g6: ArcOfCircle CenterX=0 CenterY=2e-15 CenterZ=0 NormalX=0 NormalY=0 NormalZ=1 AngleXU=0 Radius=20.4 StartAngle=6.00103 EndAngle=6.56534
  constraints (17):
    c: Diameter(g1) = 53.24
    c: Diameter(g2) = 40.8
    c: Coincident(g3,g4)
    c: Coincident(g4,g5)
    c: Coincident(g0,g2)
    c: Vertical(g4)
    c: DistanceX(g-1,g4) = 23.46
    c: Coincident(g6,g0)
    c: Coincident(g6,g3)
    c: Coincident(g6,g5)
    c: Diameter(g6) = 40.8
    c: Symmetric(g3,g5,g-1)
    c: DistanceY(g5,g3) = 11.3598
    c: Horizontal(g5)
    c: Horizontal(g3)
    c: Coincident(g1,g6)
    c: Coincident(g-1,g6)
FEATURE [PartDesign::SubtractiveLoft] SubtractiveLoft  label="PetalBodySubtractiveLoft"
  BaseFeature = -> Pad012
  Closed = false
  Placement = pos=(0,0,0) rot=(0.57735,0.57735,0.57735;2.0944rad)
  Profile = -> Sketch031
  Ruled = false
  Sections = -> [Sketch032]
FEATURE [PartDesign::PolarPattern] PolarPattern  label="ExisFixatorBodyPolarPattern"
  Angle = 360
  Axis = -> Sketch027 [N_Axis]
  BaseFeature = -> SubtractiveLoft
  Occurrences = 3
  Originals = -> [Pad012,AdditiveLoft,SubtractiveLoft]
  Placement = pos=(0,0,0) rot=(0.57735,0.57735,0.57735;2.0944rad)
FEATURE [PartDesign::Chamfer] Chamfer001
  Angle = 45
  Base = -> PolarPattern [Edge38,Edge9,Edge5,Edge23,Edge65,Edge59,Edge69,Edge47,Edge41]
  BaseFeature = -> PolarPattern
  ChamferType = 1
  FlipDirection = false
  Placement = pos=(0,0,0) rot=(0.57735,0.57735,0.57735;2.0944rad)
  Size = 2
  Size2 = 1
  SupportTransform = false
  UseAllEdges = false
FEATURE [PartDesign::Body] Body007  label="AxisFixatorBody"
  Group = -> [Sketch027,Pad012,Sketch031,Sketch032,SubtractiveLoft,PolarPattern,Chamfer001]
  Origin = -> Origin013
  Tip = -> Chamfer001
COMPONENT P5 — recipe-attached ("PetalMountingTemplate", modeled in this document).
Construction recipe (the document's own serialized feature program — sketch geometry with constraints, then the solid features built on it; lengths are millimeters unless a unit is written):

FEATURE [Sketcher::SketchObject] Sketch035  label="CommonFixatorScatch001"
  AttachmentOffset = pos=(0,0,16.32) rot=(0,0,1;0rad)
  FullyConstrained = false
  MapMode = 5
  Placement = pos=(16.32,-3.6e-15,3.6e-15) rot=(0.57735,0.57735,0.57735;2.0944rad)
  Support = -> [YZ_Plane013]
  expr: .AttachmentOffset.Base.z = Spreadsheet.mmFixatorHight * 0.8
  expr: Constraints[0] = Spreadsheet.mmAxisTubeDia + 2 * Spreadsheet.mmFixatorThick
  expr: Constraints[24] = Spreadsheet.mmBaseWidth
  expr: Constraints[3] = Spreadsheet.mmAxisTubeDia
  sketch-geometry (9):
    g0: Circle CenterX=0 CenterY=0 CenterZ=0 NormalX=0 NormalY=0 NormalZ=1 AngleXU=0 Radius=26.62
    g1: LineSegment StartX=0 StartY=0 StartZ=0 EndX=49.303 EndY=28.4651 EndZ=0
    g2: ArcOfCircle CenterX=0 CenterY=0 CenterZ=0 NormalX=0 NormalY=0 NormalZ=1 AngleXU=0 Radius=20.4 StartAngle=4.71235 EndAngle=6.7955
    g3: LineSegment StartX=0 StartY=-20.4 StartZ=0 EndX=0 EndY=-39.1443 EndZ=0
    g4: LineSegment StartX=0 StartY=-39.1443 StartZ=0 EndX=6.1036 EndY=-42.6683 EndZ=0
    g5: LineSegment StartX=6.1036 StartY=-42.6683 StartZ=0 EndX=40.0036 EndY=16.0483 EndZ=0
    g6: LineSegment StartX=40.0036 StartY=16.0483 StartZ=0 EndX=33.9 EndY=19.5722 EndZ=0
    g7: LineSegment StartX=33.9 StartY=19.5722 StartZ=0 EndX=17.6669 EndY=10.2 EndZ=0
    g8: ArcOfCircle CenterX=0 CenterY=0 CenterZ=0 NormalX=0 NormalY=0 NormalZ=1 AngleXU=0 Radius=20.4 StartAngle=4.71239 EndAngle=6.80678
  constraints (25):
    c: Diameter(g0) = 53.24
    c: Angle(g-1,g1) = 0.523599
    c: PointOnObject(g6,g1)
    c: Diameter(g2) = 40.8
    c: Vertical(g3)
    c: Coincident(g3,g4)
    c: Coincident(g4,g5)
    c: Coincident(g5,g6)
    c: Coincident(g6,g7)
    c: PointOnObject(g3,g-2)
    c: Parallel(g4,g6)
    c: Perpendicular(g5,g4)
    c: Tangent(g0,g5)
    c: PointOnObject(g8,g1)
    c: Coincident(g8,g7)
    c: PointOnObject(g8,g-2)
    c: PointOnObject(g8,g-1)
    c: PointOnObject(g8,g2)
    c: Coincident(g3,g8)
    c: Equal(g4,g6)
    c: Equal(g7,g3)
    c: Coincident(g2,g1)
    c: Coincident(g8,g1)
    c: Coincident(g8,g0)
    c: Distance(g4,g5) = 67.8
FEATURE [PartDesign::Pad] Pad013  label="AxisFixatorBodyPad001"
  Direction = (1,-2e-16,3e-16)
  Length = 6.12
  Length2 = 10
  Placement = pos=(0,0,0) rot=(0.57735,0.57735,0.57735;2.0944rad)
  Profile = -> Sketch035
  ReferenceAxis = -> Sketch035 [N_Axis]
  Type = 0
  expr: Length = Spreadsheet.mmFixatorHight * 0.3
FEATURE [Sketcher::SketchObject] Sketch038  label="MaxPetalBase004"
  FullyConstrained = false
  MapMode = 5
  Placement = pos=(0,0,0) rot=(0.57735,0.57735,0.57735;2.0944rad)
  Support = -> [YZ_Plane013]
  expr: Constraints[0] = Spreadsheet.mmAxisTubeDia + 2 * Spreadsheet.mmFixatorThick
  expr: Constraints[10] = Spreadsheet.mmAxisTubeDia
  expr: Constraints[15] = Spreadsheet.mmPetalPocketWidth
  expr: Constraints[1] = Spreadsheet.mmAxisTubeDia
  expr: Constraints[6] = Spreadsheet.mmAxisTubeDia * 2
  sketch-geometry (7):
    g0: Circle CenterX=0 CenterY=2.5e-15 CenterZ=0 NormalX=0 NormalY=0 NormalZ=1 AngleXU=0 Radius=39.855
    g1: Circle CenterX=0 CenterY=-1.1e-15 CenterZ=0 NormalX=0 NormalY=0 NormalZ=1 AngleXU=0 Radius=26.62
    g2: ArcOfCircle CenterX=0 CenterY=2.5e-15 CenterZ=0 NormalX=0 NormalY=0 NormalZ=1 AngleXU=0 Radius=20.4 StartAngle=5.6709 EndAngle=6.80795
    g3: LineSegment StartX=19.5933 StartY=5.67991 StartZ=0 EndX=81.6 EndY=5.67991 EndZ=0
    g4: LineSegment StartX=81.6 StartY=5.67991 StartZ=0 EndX=81.6 EndY=-5.67991 EndZ=0
    g5: LineSegment StartX=81.6 StartY=-5.67991 StartZ=0 EndX=19.5933 EndY=-5.67991 EndZ=0
    g6: ArcOfCircle CenterX=0 CenterY=2.5e-15 CenterZ=0 NormalX=0 NormalY=0 NormalZ=1 AngleXU=0 Radius=20.4 StartAngle=6.00103 EndAngle=6.56534
  constraints (16):
    c: Diameter(g1) = 53.24
    c: Diameter(g2) = 40.8
    c: Coincident(g3,g4)
    c: Coincident(g4,g5)
    c: Coincident(g0,g2)
    c: Vertical(g4)
    c: DistanceX(g-1,g4) = 81.6
    c: Coincident(g6,g0)
    c: Coincident(g6,g3)
    c: Coincident(g6,g5)
    c: Diameter(g6) = 40.8
    c: Horizontal(g3)
    c: Horizontal(g5)
    c: PointOnObject(g6,g-2)
    c: Symmetric(g3,g5,g-1)
    c: DistanceY(g5,g3) = 11.3598
FEATURE [Sketcher::SketchObject] Sketch039  label="MinPetalBase003"
  AttachmentOffset = pos=(0,0,20.4) rot=(0,0,1;0rad)
  FullyConstrained = false
  MapMode = 5
  Placement = pos=(20.4,-4.5e-15,4.5e-15) rot=(0.57735,0.57735,0.57735;2.0944rad)
  Support = -> [YZ_Plane013]
  expr: .AttachmentOffset.Base.z = Spreadsheet.mmFixatorHight
  expr: Constraints[0] = Spreadsheet.mmAxisTubeDia + 2 * Spreadsheet.mmFixatorThick
  expr: Constraints[10] = Spreadsheet.mmAxisTubeDia
  expr: Constraints[11] = Spreadsheet.mmPetalPocketWidth
  expr: Constraints[1] = Spreadsheet.mmAxisTubeDia
  expr: Constraints[6] = Spreadsheet.mmAxisTubeDia * 2
  sketch-geometry (7):
    g0: Circle CenterX=0 CenterY=2.1e-15 CenterZ=0 NormalX=0 NormalY=0 NormalZ=1 AngleXU=0 Radius=39.844
    g1: Circle CenterX=0 CenterY=2.1e-15 CenterZ=0 NormalX=0 NormalY=0 NormalZ=1 AngleXU=0 Radius=26.62
    g2: ArcOfCircle CenterX=0 CenterY=2.1e-15 CenterZ=0 NormalX=0 NormalY=0 NormalZ=1 AngleXU=0 Radius=20.4 StartAngle=3.90517 EndAngle=6.76925
    g3: LineSegment StartX=19.5933 StartY=5.67991 StartZ=0 EndX=81.6 EndY=5.67991 EndZ=0
    g4: LineSegment StartX=81.6 StartY=5.67991 StartZ=0 EndX=81.6 EndY=-5.67991 EndZ=0
    g5: LineSegment StartX=81.6 StartY=-5.67991 StartZ=0 EndX=19.5933 EndY=-5.67991 EndZ=0
    g6: ArcOfCircle CenterX=0 CenterY=2.1e-15 CenterZ=0 NormalX=0 NormalY=0 NormalZ=1 AngleXU=0 Radius=20.4 StartAngle=6.00103 EndAngle=6.56534
  constraints (17):
    c: Diameter(g1) = 53.24
    c: Diameter(g2) = 40.8
    c: Coincident(g3,g4)
    c: Coincident(g4,g5)
    c: Coincident(g0,g2)
    c: Vertical(g4)
    c: DistanceX(g-1,g4) = 81.6
    c: Coincident(g6,g0)
    c: Coincident(g6,g3)
    c: Coincident(g6,g5)
    c: Diameter(g6) = 40.8
    c: DistanceY(g5,g3) = 11.3598
    c: Symmetric(g3,g5,g-1)
    c: Coincident(g1,g6)
    c: Coincident(g-1,g6)
    c: Horizontal(g3)
    c: Horizontal(g5)
FEATURE [PartDesign::SubtractiveLoft] SubtractiveLoft001  label="PetalBodySubtractiveLoft001"
  BaseFeature = -> Pad013
  Closed = false
  Placement = pos=(0,0,0) rot=(0.57735,0.57735,0.57735;2.0944rad)
  Profile = -> Sketch038
  Ruled = false
  Sections = -> [Sketch039]
FEATURE [PartDesign::PolarPattern] PolarPattern001  label="ExisFixatorBodyPolarPattern001"
  Angle = 360
  Axis = -> Sketch035 [N_Axis]
  BaseFeature = -> SubtractiveLoft001
  Occurrences = 3
  Originals = -> [Pad013,SubtractiveLoft001]
  Placement = pos=(0,0,0) rot=(0.57735,0.57735,0.57735;2.0944rad)
FEATURE [Sketcher::SketchObject] Sketch040  label="CommonFixatorScatch002"
  AttachmentOffset = pos=(0,0,16.32) rot=(0,0,1;0rad)
  FullyConstrained = true
  MapMode = 5
  Placement = pos=(16.32,-3.6e-15,3.6e-15) rot=(0.57735,0.57735,0.57735;2.0944rad)
  Support = -> [YZ_Plane013]
  expr: .AttachmentOffset.Base.z = Spreadsheet.mmFixatorHight * 0.8
  expr: Constraints[11] = Spreadsheet.mmAxisTubeDia * 2
  expr: Constraints[14] = Spreadsheet.mmTemplatePartsConnectorDia - 2 * Spreadsheet.mmAirSpace
  expr: Constraints[15] = Spreadsheet.mmTemplatePartsConnectorDia * 3 / 2
  expr: Constraints[1] = Spreadsheet.mmAxisTubeDia + 2 * Spreadsheet.mmFixatorThick
  expr: Constraints[27] = Spreadsheet.mmAirSpace
  expr: Constraints[33] = Spreadsheet.mmTemplatePartsConnectorDia / 3
  expr: Constraints[41] = Spreadsheet.mmTemplatePartsConnectorDia
  expr: Constraints[43] = Spreadsheet.mmTemplatePartsConnectorDia * 2 / 3
  expr: Constraints[45] = Spreadsheet.mmTemplatePartsConnectorDia * 2 / 3 - 2 * Spreadsheet.mmAirSpace
  expr: Constraints[52] = Spreadsheet.mmTemplatePartsConnectorDia / 3
  expr: Constraints[55] = Spreadsheet.mmTemplatePartsConnectorDia / 2
  sketch-geometry (19):
    g0: Circle CenterX=0 CenterY=0 CenterZ=0 NormalX=0 NormalY=0 NormalZ=1 AngleXU=0 Radius=40.8
    g1: Circle CenterX=0 CenterY=0 CenterZ=0 NormalX=0 NormalY=0 NormalZ=1 AngleXU=0 Radius=26.62
    g2: LineSegment StartX=-35.5321 StartY=20.0526 StartZ=0 EndX=-28.3499 EndY=15.9059 EndZ=0
    g3: LineSegment StartX=22.767 StartY=-13.6064 StartZ=0 EndX=23.167 EndY=-12.9136 EndZ=0
    g4: LineSegment StartX=23.167 StartY=-12.9136 StartZ=0 EndX=21.4554 EndY=-11.9254 EndZ=0
    g5: LineSegment StartX=-35.1321 StartY=20.7454 StartZ=0 EndX=-35.5321 EndY=20.0526 EndZ=0
    g6: LineSegment StartX=23.0536 StartY=-13.31 StartZ=0 EndX=-35.3338 EndY=20.4 EndZ=0
    g7: ArcOfCircle CenterX=-26.42 CenterY=17.1754 CenterZ=0 NormalX=0 NormalY=0 NormalZ=1 AngleXU=0 Radius=2.31 StartAngle=4.65418 EndAngle=10.0066
    g8: LineSegment StartX=-26.5543 StartY=14.8693 StartZ=0 EndX=18.3629 EndY=-11.0637 EndZ=0
    g9: LineSegment StartX=-29.5129 StartY=17.5011 StartZ=0 EndX=-35.1321 EndY=20.7454 EndZ=0
    g10: LineSegment StartX=-35.1321 StartY=20.7454 StartZ=0 EndX=-35.5321 EndY=20.0526 EndZ=0
    g11: LineSegment StartX=-35.5321 StartY=20.0526 StartZ=0 EndX=22.851 EndY=-13.6549 EndZ=0
    g12: LineSegment StartX=22.851 StartY=-13.6549 StartZ=0 EndX=23.251 EndY=-12.9621 EndZ=0
    g13: LineSegment StartX=23.251 StartY=-12.9621 StartZ=0 EndX=-35.1321 EndY=20.7454 EndZ=0
    g14: ArcOfCircle CenterX=-26.42 CenterY=17.1754 CenterZ=0 NormalX=0 NormalY=0 NormalZ=1 AngleXU=0 Radius=3.11 StartAngle=5.34093 EndAngle=9.31984
    g15: ArcOfCircle CenterX=20.188 CenterY=-12.0474 CenterZ=0 NormalX=0 NormalY=0 NormalZ=1 AngleXU=0 Radius=2.07333 StartAngle=2.64723 EndAngle=5.73035
    g16: ArcOfCircle CenterX=20.188 CenterY=-12.0474 CenterZ=0 NormalX=0 NormalY=0 NormalZ=1 AngleXU=0 Radius=1.27333 StartAngle=1.99844 EndAngle=6.37914
    g17: LineSegment StartX=21.9524 StartY=-13.1361 StartZ=0 EndX=22.767 EndY=-13.6064 EndZ=0
    g18: LineSegment StartX=19.6599 StartY=-10.8888 StartZ=0 EndX=-24.5914 EndY=14.6597 EndZ=0
  constraints (56):
    c: PointOnObject(g6,g0)
    c: Diameter(g1) = 53.24
    c: Coincident(g0,g1)
    c: Coincident(g0,g-1)
    c: Coincident(g3,g4)
    c: Coincident(g9,g5)
    c: Coincident(g5,g2)
    c: Perpendicular(g3,g2)
    c: Symmetric(g2,g9,g6)
    c: Symmetric(g17,g3,g6)
    c: PointOnObject(g0,g6)
    c: Diameter(g0) = 81.6
    c: PointOnObject(g6,g1)
    c: Angle(g-1,g6) = 2.61799
    c: Diameter(g7) = 4.62
    c: Distance(g7,g5) = 9.33
    c: Parallel(g9,g4)
    c: Parallel(g2,g8)
    c: Coincident(g10,g11)
    c: Coincident(g11,g12)
    c: Coincident(g12,g13)
    c: Coincident(g13,g10)
    c: PointOnObject(g10,g0)
    c: Symmetric(g10,g10,g6)
    c: Parallel(g6,g13)
    c: Parallel(g11,g13)
    c: Coincident(g5,g10)
    c: Distance(g3,g3) = 0.8
    c: Coincident(g3,g17)
    c: PointOnObject(g11,g1)
    c: PointOnObject(g12,g1)
    c: PointOnObject(g3,g13)
    c: Distance(g6,g3) = 0.1
    c: Distance(g2,g8) = 2.07333
    c: PointOnObject(g14,g13)
    c: PointOnObject(g14,g13)
    c: PointOnObject(g18,g14)
    c: PointOnObject(g9,g14)
    c: Coincident(g7,g8)
    c: Coincident(g7,g2)
    c: Coincident(g14,g7)
    c: Diameter(g14) = 6.22
    c: PointOnObject(g18,g13)
    c: Diameter(g15) = 4.14667
    c: Coincident(g15,g16)
    c: Diameter(g16) = 2.54667
    c: Coincident(g15,g8)
    c: PointOnObject(g8,g11)
    c: Coincident(g17,g15)
    c: PointOnObject(g15,g11)
    c: Coincident(g4,g16)
    c: Coincident(g18,g16)
    c: Distance(g16,g4) = 2.07333
    c: PointOnObject(g4,g13)
    c: PointOnObject(g16,g13)
    c: Distance(g15,g12) = 3.11
FEATURE [PartDesign::Pocket] Pocket003
  BaseFeature = -> PolarPattern001
  Direction = (-1,2e-16,-3e-16)
  Length = 40.8
  Length2 = 5
  Midplane = true
  Placement = pos=(0,0,0) rot=(0.57735,0.57735,0.57735;2.0944rad)
  Profile = -> Sketch040
  ReferenceAxis = -> Sketch040 [N_Axis]
  Type = 0
  expr: Length = Spreadsheet.mmAxisTubeDia
FEATURE [PartDesign::Chamfer] Chamfer002
  Angle = 45
  Base = -> Pocket003 [Edge1,Edge35,Edge31,Edge98,Edge94,Edge47,Edge12]
  BaseFeature = -> Pocket003
  ChamferType = 0
  FlipDirection = false
  Placement = pos=(0,0,0) rot=(0.57735,0.57735,0.57735;2.0944rad)
  Size = 1
  Size2 = 1
  SupportTransform = false
  UseAllEdges = false
FEATURE [PartDesign::Chamfer] Chamfer003
  Angle = 45
  Base = -> Chamfer002 [Edge56,Edge17,Edge3,Edge28]
  BaseFeature = -> Chamfer002
  ChamferType = 0
  FlipDirection = false
  Placement = pos=(0,0,0) rot=(0.57735,0.57735,0.57735;2.0944rad)
  Size = 1
  Size2 = 1
  SupportTransform = false
  UseAllEdges = false
FEATURE [PartDesign::Chamfer] Chamfer004
  Angle = 45
  Base = -> Chamfer003 [Edge56,Edge61,Edge130,Edge128,Edge73,Edge75]
  BaseFeature = -> Chamfer003
  ChamferType = 0
  FlipDirection = false
  Placement = pos=(0,0,0) rot=(0.57735,0.57735,0.57735;2.0944rad)
  Size = 1
  Size2 = 1
  SupportTransform = false
  UseAllEdges = false
FEATURE [PartDesign::Fillet] Fillet
  Base = -> Chamfer004 [Edge66,Edge26]
  BaseFeature = -> Chamfer004
  Placement = pos=(0,0,0) rot=(0.57735,0.57735,0.57735;2.0944rad)
  Radius = 1
  SupportTransform = false
  UseAllEdges = false
FEATURE [PartDesign::Body] Body010  label="AxisFixatorTemplate"
  Group = -> [Sketch035,Pad013,Sketch038,Sketch039,SubtractiveLoft001,PolarPattern001,Sketch040,Pocket003,Chamfer002,Chamfer003,Chamfer004,Fillet]
  Origin = -> Origin019
  Tip = -> Fillet
COMPONENT P6 — recipe-attached ("AxisFixatorAbsolete", modeled in this document).
Construction recipe (the document's own serialized feature program — sketch geometry with constraints, then the solid features built on it; lengths are millimeters unless a unit is written):

FEATURE [Sketcher::SketchObject] Sketch041  label="CommonFixatorScatch003"
  FullyConstrained = false
  MapMode = 5
  Placement = pos=(0,0,0) rot=(0.57735,0.57735,0.57735;2.0944rad)
  Support = -> [YZ_Plane013]
  expr: Constraints[22] = 2 * (Spreadsheet.mmAxisTubeDia / 2 + Spreadsheet.mmFixatorThick) / cos(Spreadsheet.angPetal / 2)
  expr: Constraints[23] = Spreadsheet.mmHingeHight
  expr: Constraints[31] = Spreadsheet.mmAxisTubeDia
  expr: Constraints[64] = Spreadsheet.mmPetalWidth + Spreadsheet.mmAirSpace
  expr: Constraints[67] = Spreadsheet.mmAxisTubeDia / 2 + Spreadsheet.mmPetalHightMax + Spreadsheet.mmTwoSideTapeThick + Spreadsheet.mmAirSpace
  sketch-geometry (24):
    g0: LineSegment StartX=33.9 StartY=19.5722 StartZ=0 EndX=-33.9 EndY=19.5722 EndZ=0
    g1: LineSegment StartX=-33.9 StartY=19.5722 StartZ=0 EndX=0 EndY=-39.1443 EndZ=0
    g2: LineSegment StartX=0 StartY=-39.1443 StartZ=0 EndX=33.9 EndY=19.5722 EndZ=0
    g3: Circle CenterX=0 CenterY=0 CenterZ=0 NormalX=0 NormalY=0 NormalZ=1 AngleXU=0 Radius=39.1443
    g4: LineSegment StartX=-23.8668 StartY=13.7795 StartZ=0 EndX=-23.8668 EndY=-13.7795 EndZ=0
    g5: LineSegment StartX=-23.8668 StartY=-13.7795 StartZ=0 EndX=0 EndY=-27.5591 EndZ=0
    g6: LineSegment StartX=0 StartY=-27.5591 StartZ=0 EndX=23.8668 EndY=-13.7795 EndZ=0
    g7: LineSegment StartX=23.8668 StartY=-13.7795 StartZ=0 EndX=23.8668 EndY=13.7795 EndZ=0
    g8: LineSegment StartX=23.8668 StartY=13.7795 StartZ=0 EndX=0 EndY=27.5591 EndZ=0
    g9: LineSegment StartX=-1e-16 StartY=27.5591 StartZ=0 EndX=-23.8668 EndY=13.7795 EndZ=0
    g10: Circle CenterX=0 CenterY=0 CenterZ=0 NormalX=0 NormalY=0 NormalZ=1 AngleXU=0 Radius=27.5591
    g11: LineSegment StartX=0 StartY=0 StartZ=0 EndX=33.9 EndY=19.5722 EndZ=0
    g12: ArcOfCircle CenterX=0 CenterY=0 CenterZ=0 NormalX=0 NormalY=0 NormalZ=1 AngleXU=0 Radius=20.4 StartAngle=4.5996 EndAngle=6.79538
    g13: LineSegment StartX=0 StartY=-20.4 StartZ=0 EndX=0 EndY=-39.1443 EndZ=0
    g14: LineSegment StartX=0 StartY=-39.1443 StartZ=0 EndX=6.91684 EndY=-43.1378 EndZ=0
    g15: LineSegment StartX=6.91684 StartY=-43.1378 StartZ=0 EndX=40.8168 EndY=15.5787 EndZ=0
    g16: LineSegment StartX=40.8168 StartY=15.5787 StartZ=0 EndX=33.9 EndY=19.5722 EndZ=0
    g17: LineSegment StartX=33.9 StartY=19.5722 StartZ=0 EndX=17.6669 EndY=10.2 EndZ=0
    g18: LineSegment StartX=14.7156 StartY=-14.1284 StartZ=0 EndX=18.6289 EndY=-20.9065 EndZ=0
    g19: LineSegment StartX=18.6289 StartY=-20.9065 StartZ=0 EndX=8.79105 EndY=-26.5864 EndZ=0
    g20: LineSegment StartX=8.79105 StartY=-26.5864 StartZ=0 EndX=4.87772 EndY=-19.8083 EndZ=0
    g21: ArcOfCircle CenterX=0 CenterY=0 CenterZ=0 NormalX=0 NormalY=0 NormalZ=1 AngleXU=0 Radius=20.4 StartAngle=4.71239 EndAngle=4.95383
    g22: ArcOfCircle CenterX=0 CenterY=0 CenterZ=0 NormalX=0 NormalY=0 NormalZ=1 AngleXU=0 Radius=20.4 StartAngle=5.51814 EndAngle=6.80678
    g23: LineSegment StartX=0 StartY=0 StartZ=0 EndX=19.5722 EndY=-33.9 EndZ=0
  constraints (64):
    c: Coincident(g0,g1)
    c: Coincident(g1,g2)
    c: Coincident(g2,g0)
    c: Equal(g0,g1)
    c: Equal(g0,g2)
    c: PointOnObject(g0,g3)
    c: Coincident(g4,g5)
    c: Coincident(g5,g6)
    c: Coincident(g6,g7)
    c: Coincident(g7,g8)
    c: Coincident(g8,g9)
    c: Coincident(g9,g4)
    c: Equal(g4, g5-g9) x5
    c: PointOnObject(g4,g10)
    c: PointOnObject(g5,g10)
    c: PointOnObject(g6,g10)
    c: PointOnObject(g7,g10)
    c: PointOnObject(g8,g10)
    c: Diameter(g10) = 55.1181
    c: Distance(g2) = 67.8
    c: PointOnObject(g5,g-2)
    c: PointOnObject(g4,g10)
    c: Angle(g-1,g11) = 0.523599
    c: Coincident(g3,g10)
    c: Coincident(g3,g11)
    c: Coincident(g3,g-1)
    c: PointOnObject(g0,g11)
    c: Diameter(g12) = 40.8
    c: Coincident(g12,g3)
    c: Vertical(g13)
    c: Coincident(g13,g14)
    c: Coincident(g14,g15)
    c: Coincident(g15,g16)
    c: Coincident(g16,g17)
    c: Coincident(g19,g20)
    c: Coincident(g1,g13)
    c: Coincident(g0,g16)
    c: Equal(g12,g21)
    c: Coincident(g12,g21)
    c: PointOnObject(g13,g-2)
    c: PointOnObject(g13,g3)
    c: Parallel(g2,g15)
    c: Parallel(g14,g16)
    c: Perpendicular(g15,g14)
    c: Tangent(g10,g15)
    c: PointOnObject(g11,g3)
    c: Coincident(g21,g22)
    c: PointOnObject(g17,g11)
    c: Coincident(g20,g21)
    c: Coincident(g21,g13)
    c: Coincident(g22,g18)
    c: PointOnObject(g22,g11)
    c: Coincident(g22,g17)
    c: PointOnObject(g17,g11)
    c: Perpendicular(g20,g19)
    c: Perpendicular(g19,g18)
    c: Coincident(g23,g21)
    c: Angle(g23,g-2) = 2.61799
    c: PointOnObject(g23,g3)
    c: Symmetric(g20,g18,g23)
    c: Distance(g20,g18) = 11.3598
    c: Perpendicular(g23,g19)
    c: Coincident(g18,g19)
    c: Distance(g21,g19) = 27.42
FEATURE [PartDesign::Pad] Pad014  label="AxisFixatorBodyPad002"
  Direction = (1,-2e-16,3e-16)
  Length = 20.4
  Length2 = 10
  Placement = pos=(0,0,0) rot=(0.57735,0.57735,0.57735;2.0944rad)
  Profile = -> Sketch041
  ReferenceAxis = -> Sketch041 [N_Axis]
  Type = 0
  expr: Length = Spreadsheet.mmFixatorHight
FEATURE [Sketcher::SketchObject] Sketch044  label="MaxPetalBase006"
  FullyConstrained = false
  MapMode = 5
  Placement = pos=(0,0,0) rot=(0.57735,0.57735,0.57735;2.0944rad)
  Support = -> [YZ_Plane013]
  expr: Constraints[0] = Spreadsheet.mmAxisTubeDia + 2 * Spreadsheet.mmFixatorThick
  expr: Constraints[14] = Spreadsheet.mmPetalWidth + Spreadsheet.mmAirSpace
  expr: Constraints[1] = Spreadsheet.mmAxisTubeDia
  expr: Constraints[5] = Spreadsheet.mmAxisTubeDia / 2 + Spreadsheet.mmPetalHightMax
  expr: Constraints[9] = Spreadsheet.mmAxisTubeDia
  sketch-geometry (7):
    g0: Circle CenterX=0 CenterY=0 CenterZ=0 NormalX=0 NormalY=0 NormalZ=1 AngleXU=0 Radius=39.855
    g1: Circle CenterX=0 CenterY=0 CenterZ=0 NormalX=0 NormalY=0 NormalZ=1 AngleXU=0 Radius=26.62
    g2: ArcOfCircle CenterX=0 CenterY=0 CenterZ=0 NormalX=0 NormalY=0 NormalZ=1 AngleXU=0 Radius=20.4 StartAngle=5.86249 EndAngle=6.74499
    g3: LineSegment StartX=19.5933 StartY=5.67991 StartZ=0 EndX=26.52 EndY=5.67991 EndZ=0
    g4: LineSegment StartX=26.52 StartY=5.67991 StartZ=0 EndX=26.52 EndY=-5.67991 EndZ=0
    g5: LineSegment StartX=26.52 StartY=-5.67991 StartZ=0 EndX=19.5933 EndY=-5.67991 EndZ=0
    g6: ArcOfCircle CenterX=0 CenterY=0 CenterZ=0 NormalX=0 NormalY=0 NormalZ=1 AngleXU=0 Radius=20.4 StartAngle=6.00103 EndAngle=6.56534
  constraints (22):
    c: Diameter(g1) = 53.24
    c: Diameter(g2) = 40.8
    c: Coincident(g3,g4)
    c: Coincident(g4,g5)
    c: Coincident(g0,g2)
    c: DistanceX(g-1,g4) = 26.52
    c: Coincident(g6,g0)
    c: Coincident(g6,g3)
    c: Coincident(g6,g5)
    c: Diameter(g6) = 40.8
    c: Coincident(g6,g-1)
    c: Symmetric(g3,g5,g-1)
    c: Horizontal(g5)
    c: Horizontal(g3)
    c: DistanceY(g5,g3) = 11.3598
    c: Coincident(g6,g1)
    c: PointOnObject(g6,g-2)
    c: PointOnObject(g6,g-1)
    c: PointOnObject(g6,g5)
    c: PointOnObject(g6,g3)
    c: PointOnObject(g3,g6)
    c: Vertical(g4)
FEATURE [Sketcher::SketchObject] Sketch045  label="MinPetalBase005"
  AttachmentOffset = pos=(0,0,18.36) rot=(0,0,1;0rad)
  FullyConstrained = false
  MapMode = 5
  Placement = pos=(18.36,-4.1e-15,4.1e-15) rot=(0.57735,0.57735,0.57735;2.0944rad)
  Support = -> [YZ_Plane013]
  expr: .AttachmentOffset.Base.z = Spreadsheet.mmFixatorHight * 0.9
  expr: Constraints[0] = Spreadsheet.mmAxisTubeDia + 2 * Spreadsheet.mmFixatorThick
  expr: Constraints[10] = Spreadsheet.mmAxisTubeDia
  expr: Constraints[12] = Spreadsheet.mmPetalWidth + Spreadsheet.mmAirSpace
  expr: Constraints[1] = Spreadsheet.mmAxisTubeDia
  expr: Constraints[6] = Spreadsheet.mmAxisTubeDia / 2 + Spreadsheet.mmPetalHightMin
  sketch-geometry (7):
    g0: Circle CenterX=0 CenterY=2.3e-15 CenterZ=0 NormalX=0 NormalY=0 NormalZ=1 AngleXU=0 Radius=39.844
    g1: Circle CenterX=0 CenterY=2.3e-15 CenterZ=0 NormalX=0 NormalY=0 NormalZ=1 AngleXU=0 Radius=26.62
    g2: ArcOfCircle CenterX=0 CenterY=2.3e-15 CenterZ=0 NormalX=0 NormalY=0 NormalZ=1 AngleXU=0 Radius=20.4 StartAngle=3.8687 EndAngle=6.82101
    g3: LineSegment StartX=19.5933 StartY=5.67991 StartZ=0 EndX=23.46 EndY=5.67991 EndZ=0
    g4: LineSegment StartX=23.46 StartY=5.67991 StartZ=0 EndX=23.46 EndY=-5.67991 EndZ=0
    g5: LineSegment StartX=23.46 StartY=-5.67991 StartZ=0 EndX=19.5933 EndY=-5.67991 EndZ=0
    g6: ArcOfCircle CenterX=0 CenterY=2.3e-15 CenterZ=0 NormalX=0 NormalY=0 NormalZ=1 AngleXU=0 Radius=20.4 StartAngle=6.00103 EndAngle=6.56534
  constraints (17):
    c: Diameter(g1) = 53.24
    c: Diameter(g2) = 40.8
    c: Coincident(g3,g4)
    c: Coincident(g4,g5)
    c: Coincident(g0,g2)
    c: Vertical(g4)
    c: DistanceX(g-1,g4) = 23.46
    c: Coincident(g6,g0)
    c: Coincident(g6,g3)
    c: Coincident(g6,g5)
    c: Diameter(g6) = 40.8
    c: Symmetric(g3,g5,g-1)
    c: DistanceY(g5,g3) = 11.3598
    c: Horizontal(g3)
    c: Horizontal(g5)
    c: Coincident(g6,g1)
    c: Coincident(g6,g-1)
FEATURE [PartDesign::SubtractiveLoft] SubtractiveLoft002  label="PetalBodySubtractiveLoft002"
  BaseFeature = -> Pad014
  Closed = false
  Placement = pos=(0,0,0) rot=(0.57735,0.57735,0.57735;2.0944rad)
  Profile = -> Sketch044
  Ruled = false
  Sections = -> [Sketch045]
FEATURE [PartDesign::PolarPattern] PolarPattern002  label="ExisFixatorBodyPolarPattern002"
  Angle = 360
  Axis = -> Sketch041 [N_Axis]
  BaseFeature = -> SubtractiveLoft002
  Occurrences = 3
  Originals = -> [Pad014,SubtractiveLoft002]
  Placement = pos=(0,0,0) rot=(0.57735,0.57735,0.57735;2.0944rad)
FEATURE [PartDesign::Body] Body011  label="AxisFixatorBody001"
  Group = -> [Sketch041,Pad014,Sketch044,Sketch045,SubtractiveLoft002,PolarPattern002]
  Origin = -> Origin021
  Tip = -> PolarPattern002
COMPONENT P7 — recipe-attached ("PetalPart", modeled in this document).
Construction recipe (the document's own serialized feature program — sketch geometry with constraints, then the solid features built on it; lengths are millimeters unless a unit is written):

FEATURE [Sketcher::SketchObject] Sketch029  label="MaxPetalBase"
  FullyConstrained = false
  MapMode = 5
  Placement = pos=(0,0,0) rot=(0.57735,0.57735,0.57735;2.0944rad)
  Support = -> [YZ_Plane015]
  expr: Constraints[0] = Spreadsheet.mmAxisTubeDia + 2 * Spreadsheet.mmFixatorThick
  expr: Constraints[12] = Spreadsheet.mmAxisTubeDia / 2 + Spreadsheet.mmPetalHightMax
  expr: Constraints[16] = Spreadsheet.mmPetalWidth
  expr: Constraints[1] = Spreadsheet.mmAxisTubeDia
  expr: Constraints[6] = Spreadsheet.mmAxisTubeDia + Spreadsheet.mmTwoSideTapeThick * 2
  sketch-geometry (7):
    g0: Circle CenterX=0 CenterY=0 CenterZ=0 NormalX=0 NormalY=0 NormalZ=1 AngleXU=0 Radius=39.8652
    g1: Circle CenterX=0 CenterY=0 CenterZ=0 NormalX=0 NormalY=0 NormalZ=1 AngleXU=0 Radius=26.62
    g2: ArcOfCircle CenterX=0 CenterY=0 CenterZ=0 NormalX=0 NormalY=0 NormalZ=1 AngleXU=0 Radius=20.4 StartAngle=3.89684 EndAngle=6.80091
    g3: LineSegment StartX=19.8084 StartY=5.27991 StartZ=0 EndX=26.52 EndY=5.27991 EndZ=0
    g4: LineSegment StartX=26.52 StartY=5.27991 StartZ=0 EndX=26.52 EndY=-5.27991 EndZ=0
    g5: LineSegment StartX=26.52 StartY=-5.27991 StartZ=0 EndX=19.8084 EndY=-5.27991 EndZ=0
    g6: ArcOfCircle CenterX=0 CenterY=0 CenterZ=0 NormalX=0 NormalY=0 NormalZ=1 AngleXU=0 Radius=20.5 StartAngle=6.02269 EndAngle=6.54368
  constraints (20):
    c: Diameter(g1) = 53.24
    c: Diameter(g2) = 40.8
    c: Coincident(g3,g4)
    c: Coincident(g4,g5)
    c: PointOnObject(g3,g2)
    c: Coincident(g6,g0)
    c: Diameter(g6) = 41
    c: Coincident(g1,g6)
    c: Coincident(g0,g2)
    c: Vertical(g4)
    c: PointOnObject(g3,g6)
    c: PointOnObject(g5,g6)
    c: DistanceX(g-1,g4) = 26.52
    c: Horizontal(g3)
    c: Horizontal(g5)
    c: Symmetric(g5,g3,g-1)
    c: DistanceY(g5,g3) = 10.5598
    c: Coincident(g-1,g6)
    c: PointOnObject(g6,g5)
    c: PointOnObject(g6,g3)
FEATURE [Sketcher::SketchObject] Sketch030  label="MinPetalBase"
  AttachmentOffset = pos=(0,0,20.4) rot=(0,0,1;0rad)
  FullyConstrained = false
  MapMode = 5
  Placement = pos=(20.4,-4.5e-15,4.5e-15) rot=(0.57735,0.57735,0.57735;2.0944rad)
  Support = -> [YZ_Plane015]
  expr: .AttachmentOffset.Base.z = Spreadsheet.mmFixatorHight
  expr: Constraints[0] = Spreadsheet.mmAxisTubeDia + 2 * Spreadsheet.mmFixatorThick
  expr: Constraints[11] = Spreadsheet.mmAxisTubeDia / 2 + Spreadsheet.mmPetalHightMin
  expr: Constraints[15] = Spreadsheet.mmPetalWidth
  expr: Constraints[1] = Spreadsheet.mmAxisTubeDia
  expr: Constraints[5] = Spreadsheet.mmAxisTubeDia + Spreadsheet.mmTwoSideTapeThick * 2
  sketch-geometry (7):
    g0: Circle CenterX=0 CenterY=1.8e-15 CenterZ=0 NormalX=0 NormalY=0 NormalZ=1 AngleXU=0 Radius=39.865
    g1: Circle CenterX=0 CenterY=1.8e-15 CenterZ=0 NormalX=0 NormalY=0 NormalZ=1 AngleXU=0 Radius=26.62
    g2: ArcOfCircle CenterX=0 CenterY=1.8e-15 CenterZ=0 NormalX=0 NormalY=0 NormalZ=1 AngleXU=0 Radius=20.4 StartAngle=3.86544 EndAngle=6.7404
    g3: LineSegment StartX=19.8084 StartY=5.27991 StartZ=0 EndX=23.46 EndY=5.27991 EndZ=0
    g4: LineSegment StartX=23.46 StartY=5.27991 StartZ=0 EndX=23.46 EndY=-5.27991 EndZ=0
    g5: LineSegment StartX=23.46 StartY=-5.27991 StartZ=0 EndX=19.8084 EndY=-5.27991 EndZ=0
    g6: ArcOfCircle CenterX=0 CenterY=1.8e-15 CenterZ=0 NormalX=0 NormalY=0 NormalZ=1 AngleXU=0 Radius=20.5 StartAngle=6.02269 EndAngle=6.54368
  constraints (20):
    c: Diameter(g1) = 53.24
    c: Diameter(g2) = 40.8
    c: Coincident(g3,g4)
    c: Coincident(g4,g5)
    c: Coincident(g6,g0)
    c: Diameter(g6) = 41
    c: Coincident(g1,g6)
    c: Coincident(g0,g2)
    c: Vertical(g4)
    c: PointOnObject(g3,g6)
    c: PointOnObject(g5,g6)
    c: DistanceX(g-1,g4) = 23.46
    c: PointOnObject(g6,g5)
    c: PointOnObject(g6,g3)
    c: Coincident(g6,g-1)
    c: DistanceY(g5,g3) = 10.5598
    c: Symmetric(g5,g3,g-1)
    c: Horizontal(g3)
    c: Horizontal(g5)
    c: PointOnObject(g6,g-2)
FEATURE [PartDesign::AdditiveLoft] AdditiveLoft  label="PetalBodyBodyAdditiveLoft"
  Closed = false
  Placement = pos=(0,0,0) rot=(0.57735,0.57735,0.57735;2.0944rad)
  Profile = -> Sketch029
  Ruled = false
  Sections = -> [Sketch030]
FEATURE [PartDesign::Chamfer] Chamfer
  Angle = 45
  Base = -> AdditiveLoft [Edge8,Edge9,Edge6,Edge3,Edge2,Edge1,Edge11,Edge5]
  BaseFeature = -> AdditiveLoft
  ChamferType = 0
  FlipDirection = false
  Placement = pos=(0,0,0) rot=(0.57735,0.57735,0.57735;2.0944rad)
  Size = 1
  Size2 = 1
  SupportTransform = false
  UseAllEdges = false
FEATURE [PartDesign::Body] Body008  label="PetalBodyPart"
  Group = -> [Sketch029,Sketch030,AdditiveLoft,Chamfer]
  Origin = -> Origin015
  Tip = -> Chamfer
PROVENANCE & LICENSES
A FreeCAD (.FCStd) document from a public repository crawl; recipes are the document's own serialized feature recipes (and, for linked parts, companion documents' recipes).
License: as declared in the source repository (recorded in the dataset sidecar).
